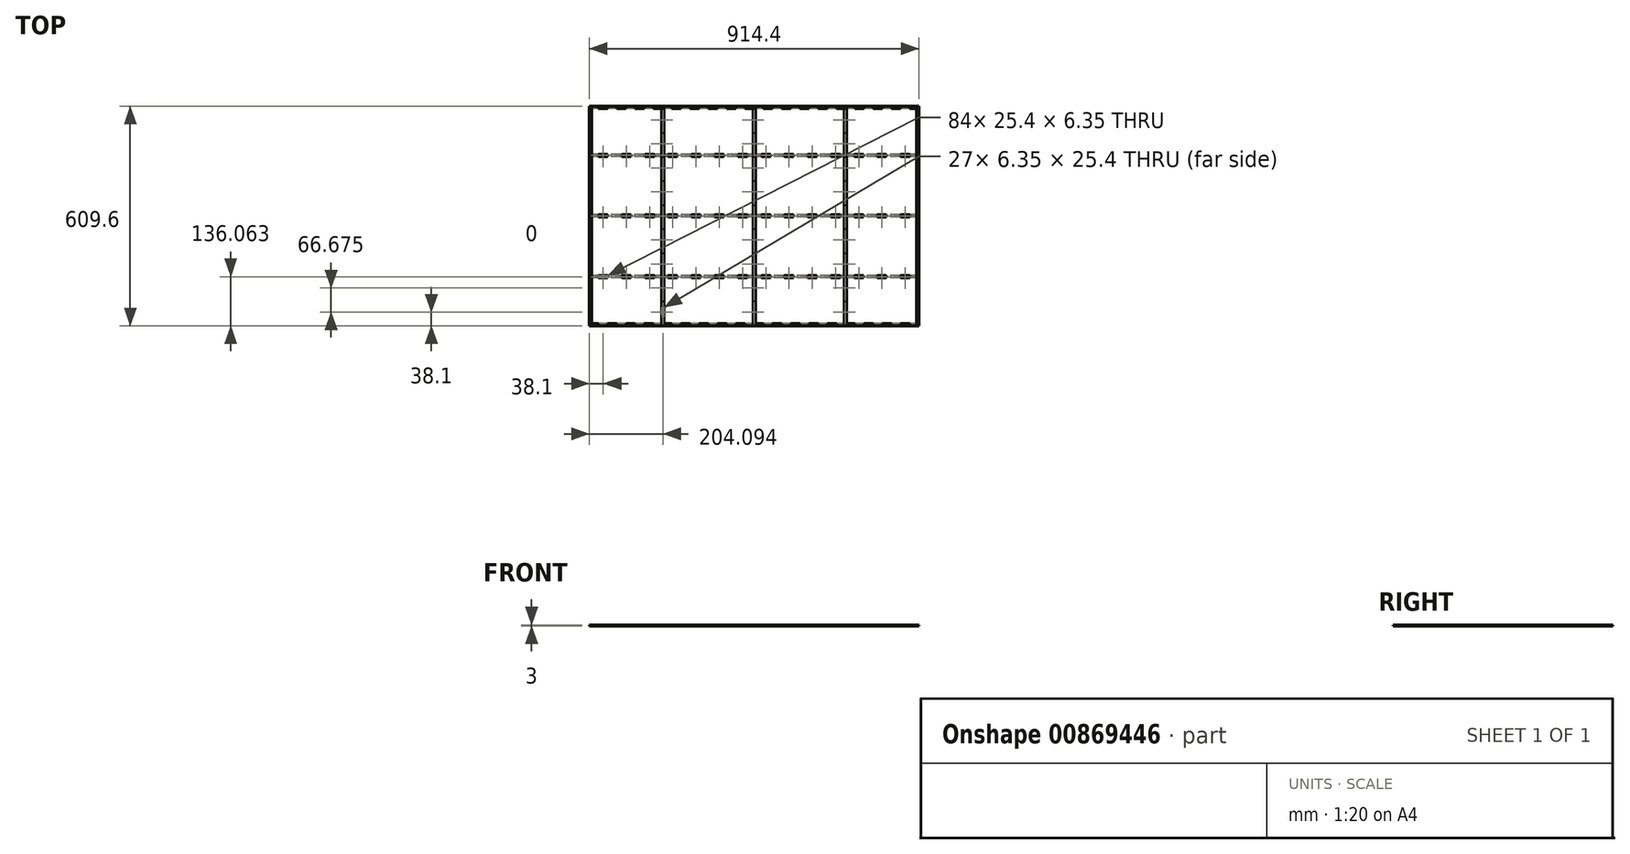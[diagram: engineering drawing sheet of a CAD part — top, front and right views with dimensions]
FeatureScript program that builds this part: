
annotation { "Feature Type Name" : "Feature", "Feature Type Description" : "" }
export const myFeature = defineFeature(function(context is Context, id is Id, definition is map)
    precondition{}
    {
        {
            assignVariable(context, id + "F0", {"name" : "thick", "anyValue" : 0.25});
        }
        {
            assignVariable(context, id + "F1", {"name" : "height", "anyValue" : 3});
        }
        {
            var Q0;
            Q0=qCreatedBy(makeId("Top.planeOp"),FACE);
            var sketch = newSketch(context, id + "F2", { "sketchPlane" : qUnion([Q0])});
            skLineSegment(sketch, "E0.bottom", {"start": v(-457.2, 304.8) * mm, "end": v(457.2, 304.8) * mm, "construction": true});
            skLineSegment(sketch, "E0.top", {"start": v(-457.2, -304.8) * mm, "end": v(457.2, -304.8) * mm, "construction": true});
            skLineSegment(sketch, "E0.left", {"start": v(-457.2, 304.8) * mm, "end": v(-457.2, -304.8) * mm, "construction": true});
            skLineSegment(sketch, "E0.right", {"start": v(457.2, 304.8) * mm, "end": v(457.2, -304.8) * mm, "construction": true});
            skPoint(sketch, "E0.middle", {"position": v(0, 0) * mm});
            skLineSegment(sketch, "E1.bottom", {"start": v(-253.1, 168.74) * mm, "end": v(253.1, 168.74) * mm, "construction": true});
            skLineSegment(sketch, "E1.top", {"start": v(-253.1, -168.74) * mm, "end": v(253.1, -168.74) * mm, "construction": true});
            skLineSegment(sketch, "E1.left", {"start": v(-253.1, 168.74) * mm, "end": v(-253.1, -168.74) * mm, "construction": true});
            skLineSegment(sketch, "E1.right", {"start": v(253.1, 168.74) * mm, "end": v(253.1, -168.74) * mm, "construction": true});
            skLineSegment(sketch, "E2", {"start": v(-457.2, 0) * mm, "end": v(457.2, 0) * mm, "construction": true});
            skLineSegment(sketch, "E3", {"start": v(0, 304.8) * mm, "end": v(0, -304.8) * mm, "construction": true});
            skLineSegment(sketch, "E4", {"start": v(-253.1, 304.8) * mm, "end": v(-253.1, -304.8) * mm, "construction": true});
            skLineSegment(sketch, "E5", {"start": v(253.1, -304.8) * mm, "end": v(253.1, 304.8) * mm, "construction": true});
            skLineSegment(sketch, "E6", {"start": v(457.2, 168.74) * mm, "end": v(-457.2, 168.74) * mm, "construction": true});
            skLineSegment(sketch, "E7", {"start": v(457.2, -168.74) * mm, "end": v(-457.2, -168.74) * mm, "construction": true});
            skSolve(sketch);
        }
        {
            var Q0;
            Q0=qCreatedBy(makeId("Top.planeOp"),FACE);
            var sketch = newSketch(context, id + "F3", { "sketchPlane" : qUnion([Q0])});
            skLineSegment(sketch, "E8.bottom", {"start": v(-256.28, 304.8) * mm, "end": v(-249.93, 304.8) * mm});
            skLineSegment(sketch, "E8.top", {"start": v(-256.28, -304.8) * mm, "end": v(-249.93, -304.8) * mm});
            skLineSegment(sketch, "E8.left", {"start": v(-256.28, 304.8) * mm, "end": v(-256.28, -304.8) * mm});
            skLineSegment(sketch, "E8.right", {"start": v(-249.93, 304.8) * mm, "end": v(-249.93, -304.8) * mm});
            skPoint(sketch, "E8.middle", {"position": v(-253.1, 0) * mm});
            skLineSegment(sketch, "E9.bottom", {"start": v(-3.17, 304.8) * mm, "end": v(3.17, 304.8) * mm});
            skLineSegment(sketch, "E9.top", {"start": v(-3.18, -304.8) * mm, "end": v(3.18, -304.8) * mm});
            skLineSegment(sketch, "E9.left", {"start": v(-3.17, 304.8) * mm, "end": v(-3.18, -304.8) * mm});
            skLineSegment(sketch, "E9.right", {"start": v(3.18, 304.8) * mm, "end": v(3.17, -304.8) * mm});
            skPoint(sketch, "E9.middle", {"position": v(0, 0) * mm});
            skLineSegment(sketch, "E10.bottom", {"start": v(256.28, 304.8) * mm, "end": v(249.93, 304.8) * mm});
            skLineSegment(sketch, "E10.top", {"start": v(256.28, -304.8) * mm, "end": v(249.93, -304.8) * mm});
            skLineSegment(sketch, "E10.left", {"start": v(256.28, 304.8) * mm, "end": v(256.28, -304.8) * mm});
            skLineSegment(sketch, "E10.right", {"start": v(249.93, 304.8) * mm, "end": v(249.93, -304.8) * mm});
            skPoint(sketch, "E10.middle", {"position": v(253.1, 0) * mm});
            skLineSegment(sketch, "E11.bottom", {"start": v(-457.2, 304.8) * mm, "end": v(-450.85, 304.8) * mm});
            skLineSegment(sketch, "E11.top", {"start": v(-457.2, -304.8) * mm, "end": v(-450.85, -304.8) * mm});
            skLineSegment(sketch, "E11.left", {"start": v(-457.2, 304.8) * mm, "end": v(-457.2, -304.8) * mm});
            skLineSegment(sketch, "E11.right", {"start": v(-450.85, 304.8) * mm, "end": v(-450.85, -304.8) * mm});
            skPoint(sketch, "E11.middle", {"position": v(-454.03, 0) * mm});
            skLineSegment(sketch, "E12.bottom", {"start": v(457.2, 304.8) * mm, "end": v(450.85, 304.8) * mm});
            skLineSegment(sketch, "E12.top", {"start": v(457.2, -304.8) * mm, "end": v(450.85, -304.8) * mm});
            skLineSegment(sketch, "E12.left", {"start": v(457.2, 304.8) * mm, "end": v(457.2, -304.8) * mm});
            skLineSegment(sketch, "E12.right", {"start": v(450.85, 304.8) * mm, "end": v(450.85, -304.8) * mm});
            skPoint(sketch, "E12.middle", {"position": v(454.03, 0) * mm});
            skSolve(sketch);
        }
        {
            var Q0;
            Q0=qCreatedBy(makeId("Top.planeOp"),FACE);
            var sketch = newSketch(context, id + "F4", { "sketchPlane" : qUnion([Q0])});
            skLineSegment(sketch, "E13.bottom", {"start": v(-457.2, 298.45) * mm, "end": v(457.2, 298.45) * mm});
            skLineSegment(sketch, "E13.top", {"start": v(-457.2, 304.8) * mm, "end": v(457.2, 304.8) * mm});
            skLineSegment(sketch, "E13.left", {"start": v(-457.2, 298.45) * mm, "end": v(-457.2, 304.8) * mm});
            skLineSegment(sketch, "E13.right", {"start": v(457.2, 298.45) * mm, "end": v(457.2, 304.8) * mm});
            skPoint(sketch, "E13.middle", {"position": v(0, 301.62) * mm});
            skLineSegment(sketch, "E14.bottom", {"start": v(-457.2, 171.91) * mm, "end": v(457.2, 171.91) * mm});
            skLineSegment(sketch, "E14.top", {"start": v(-457.2, 165.56) * mm, "end": v(457.2, 165.56) * mm});
            skLineSegment(sketch, "E14.left", {"start": v(-457.2, 171.91) * mm, "end": v(-457.2, 165.56) * mm});
            skLineSegment(sketch, "E14.right", {"start": v(457.2, 171.91) * mm, "end": v(457.2, 165.56) * mm});
            skPoint(sketch, "E14.middle", {"position": v(0, 168.74) * mm});
            skLineSegment(sketch, "E15.bottom", {"start": v(-457.2, 3.18) * mm, "end": v(457.2, 3.18) * mm});
            skLineSegment(sketch, "E15.top", {"start": v(-457.2, -3.18) * mm, "end": v(457.2, -3.18) * mm});
            skLineSegment(sketch, "E15.left", {"start": v(-457.2, 3.18) * mm, "end": v(-457.2, -3.18) * mm});
            skLineSegment(sketch, "E15.right", {"start": v(457.2, 3.18) * mm, "end": v(457.2, -3.18) * mm});
            skPoint(sketch, "E15.middle", {"position": v(0, 0) * mm});
            skLineSegment(sketch, "E16.bottom", {"start": v(-457.2, -171.91) * mm, "end": v(457.2, -171.91) * mm});
            skLineSegment(sketch, "E16.top", {"start": v(-457.2, -165.56) * mm, "end": v(457.2, -165.56) * mm});
            skLineSegment(sketch, "E16.left", {"start": v(-457.2, -171.91) * mm, "end": v(-457.2, -165.56) * mm});
            skLineSegment(sketch, "E16.right", {"start": v(457.2, -171.91) * mm, "end": v(457.2, -165.56) * mm});
            skPoint(sketch, "E16.middle", {"position": v(0, -168.74) * mm});
            skPoint(sketch, "E16.middle.positionSnap0", {"position": v(0, -3.18) * mm});
            skPoint(sketch, "E16.centerSnap0", {"position": v(0, -3.18) * mm});
            skLineSegment(sketch, "E17.bottom", {"start": v(-457.2, -304.8) * mm, "end": v(457.2, -304.8) * mm});
            skLineSegment(sketch, "E17.top", {"start": v(-457.2, -298.45) * mm, "end": v(457.2, -298.45) * mm});
            skLineSegment(sketch, "E17.left", {"start": v(-457.2, -304.8) * mm, "end": v(-457.2, -298.45) * mm});
            skLineSegment(sketch, "E17.right", {"start": v(457.2, -304.8) * mm, "end": v(457.2, -298.45) * mm});
            skPoint(sketch, "E17.middle", {"position": v(0, -301.62) * mm});
            skSolve(sketch);
        }
        {
            var Q0;
            Q0=qCreatedBy(makeId("Top.planeOp"),FACE);
            var sketch = newSketch(context, id + "F5", { "sketchPlane" : qUnion([Q0])});
            skLineSegment(sketch, "E18.bottom", {"start": v(450.85, 298.45) * mm, "end": v(-450.85, 298.45) * mm});
            skLineSegment(sketch, "E18.top", {"start": v(450.85, -298.45) * mm, "end": v(-450.85, -298.45) * mm});
            skLineSegment(sketch, "E18.left", {"start": v(450.85, 298.45) * mm, "end": v(450.85, -298.45) * mm});
            skLineSegment(sketch, "E18.right", {"start": v(-450.85, 298.45) * mm, "end": v(-450.85, -298.45) * mm});
            skPoint(sketch, "E18.middle", {"position": v(0, 0) * mm});
            skLineSegment(sketch, "E19.bottom", {"start": v(-457.2, 304.8) * mm, "end": v(-431.8, 304.8) * mm});
            skLineSegment(sketch, "E19.top", {"start": v(-457.2, 298.45) * mm, "end": v(-431.8, 298.45) * mm});
            skLineSegment(sketch, "E19.left", {"start": v(-457.2, 304.8) * mm, "end": v(-457.2, 298.45) * mm});
            skLineSegment(sketch, "E19.right", {"start": v(-431.8, 304.8) * mm, "end": v(-431.8, 298.45) * mm});
            skLineSegment(sketch, "E20.1.0.0", {"start": v(-406.4, 304.8) * mm, "end": v(-406.4, 298.45) * mm});
            skLineSegment(sketch, "E20.1.0.1", {"start": v(-406.4, 304.8) * mm, "end": v(-381, 304.8) * mm});
            skLineSegment(sketch, "E20.1.0.2", {"start": v(-381, 304.8) * mm, "end": v(-381, 298.45) * mm});
            skLineSegment(sketch, "E20.1.0.3", {"start": v(-406.4, 298.45) * mm, "end": v(-381, 298.45) * mm});
            skLineSegment(sketch, "E20.2.0.0", {"start": v(-355.6, 304.8) * mm, "end": v(-355.6, 298.45) * mm});
            skLineSegment(sketch, "E20.2.0.1", {"start": v(-355.6, 304.8) * mm, "end": v(-330.2, 304.8) * mm});
            skLineSegment(sketch, "E20.2.0.2", {"start": v(-330.2, 304.8) * mm, "end": v(-330.2, 298.45) * mm});
            skLineSegment(sketch, "E20.2.0.3", {"start": v(-355.6, 298.45) * mm, "end": v(-330.2, 298.45) * mm});
            skLineSegment(sketch, "E20.3.0.0", {"start": v(-304.8, 304.8) * mm, "end": v(-304.8, 298.45) * mm});
            skLineSegment(sketch, "E20.3.0.1", {"start": v(-304.8, 304.8) * mm, "end": v(-279.4, 304.8) * mm});
            skLineSegment(sketch, "E20.3.0.2", {"start": v(-279.4, 304.8) * mm, "end": v(-279.4, 298.45) * mm});
            skLineSegment(sketch, "E20.3.0.3", {"start": v(-304.8, 298.45) * mm, "end": v(-279.4, 298.45) * mm});
            skLineSegment(sketch, "E20.4.0.0", {"start": v(-254, 304.8) * mm, "end": v(-254, 298.45) * mm});
            skLineSegment(sketch, "E20.4.0.1", {"start": v(-254, 304.8) * mm, "end": v(-228.6, 304.8) * mm});
            skLineSegment(sketch, "E20.4.0.2", {"start": v(-228.6, 304.8) * mm, "end": v(-228.6, 298.45) * mm});
            skLineSegment(sketch, "E20.4.0.3", {"start": v(-254, 298.45) * mm, "end": v(-228.6, 298.45) * mm});
            skLineSegment(sketch, "E20.5.0.0", {"start": v(-203.2, 304.8) * mm, "end": v(-203.2, 298.45) * mm});
            skLineSegment(sketch, "E20.5.0.1", {"start": v(-203.2, 304.8) * mm, "end": v(-177.8, 304.8) * mm});
            skLineSegment(sketch, "E20.5.0.2", {"start": v(-177.8, 304.8) * mm, "end": v(-177.8, 298.45) * mm});
            skLineSegment(sketch, "E20.5.0.3", {"start": v(-203.2, 298.45) * mm, "end": v(-177.8, 298.45) * mm});
            skLineSegment(sketch, "E20.6.0.0", {"start": v(-152.4, 304.8) * mm, "end": v(-152.4, 298.45) * mm});
            skLineSegment(sketch, "E20.6.0.1", {"start": v(-152.4, 304.8) * mm, "end": v(-127, 304.8) * mm});
            skLineSegment(sketch, "E20.6.0.2", {"start": v(-127, 304.8) * mm, "end": v(-127, 298.45) * mm});
            skLineSegment(sketch, "E20.6.0.3", {"start": v(-152.4, 298.45) * mm, "end": v(-127, 298.45) * mm});
            skLineSegment(sketch, "E20.7.0.0", {"start": v(-101.6, 304.8) * mm, "end": v(-101.6, 298.45) * mm});
            skLineSegment(sketch, "E20.7.0.1", {"start": v(-101.6, 304.8) * mm, "end": v(-76.2, 304.8) * mm});
            skLineSegment(sketch, "E20.7.0.2", {"start": v(-76.2, 304.8) * mm, "end": v(-76.2, 298.45) * mm});
            skLineSegment(sketch, "E20.7.0.3", {"start": v(-101.6, 298.45) * mm, "end": v(-76.2, 298.45) * mm});
            skLineSegment(sketch, "E20.8.0.0", {"start": v(-50.8, 304.8) * mm, "end": v(-50.8, 298.45) * mm});
            skLineSegment(sketch, "E20.8.0.1", {"start": v(-50.8, 304.8) * mm, "end": v(-25.4, 304.8) * mm});
            skLineSegment(sketch, "E20.8.0.2", {"start": v(-25.4, 304.8) * mm, "end": v(-25.4, 298.45) * mm});
            skLineSegment(sketch, "E20.8.0.3", {"start": v(-50.8, 298.45) * mm, "end": v(-25.4, 298.45) * mm});
            skLineSegment(sketch, "E20.9.0.0", {"start": v(0, 304.8) * mm, "end": v(0, 298.45) * mm});
            skLineSegment(sketch, "E20.9.0.1", {"start": v(0, 304.8) * mm, "end": v(25.4, 304.8) * mm});
            skLineSegment(sketch, "E20.9.0.2", {"start": v(25.4, 304.8) * mm, "end": v(25.4, 298.45) * mm});
            skLineSegment(sketch, "E20.9.0.3", {"start": v(0, 298.45) * mm, "end": v(25.4, 298.45) * mm});
            skLineSegment(sketch, "E20.10.0.0", {"start": v(50.8, 304.8) * mm, "end": v(50.8, 298.45) * mm});
            skLineSegment(sketch, "E20.10.0.1", {"start": v(50.8, 304.8) * mm, "end": v(76.2, 304.8) * mm});
            skLineSegment(sketch, "E20.10.0.2", {"start": v(76.2, 304.8) * mm, "end": v(76.2, 298.45) * mm});
            skLineSegment(sketch, "E20.10.0.3", {"start": v(50.8, 298.45) * mm, "end": v(76.2, 298.45) * mm});
            skLineSegment(sketch, "E20.11.0.0", {"start": v(101.6, 304.8) * mm, "end": v(101.6, 298.45) * mm});
            skLineSegment(sketch, "E20.11.0.1", {"start": v(101.6, 304.8) * mm, "end": v(127, 304.8) * mm});
            skLineSegment(sketch, "E20.11.0.2", {"start": v(127, 304.8) * mm, "end": v(127, 298.45) * mm});
            skLineSegment(sketch, "E20.11.0.3", {"start": v(101.6, 298.45) * mm, "end": v(127, 298.45) * mm});
            skLineSegment(sketch, "E20.12.0.0", {"start": v(152.4, 304.8) * mm, "end": v(152.4, 298.45) * mm});
            skLineSegment(sketch, "E20.12.0.1", {"start": v(152.4, 304.8) * mm, "end": v(177.8, 304.8) * mm});
            skLineSegment(sketch, "E20.12.0.2", {"start": v(177.8, 304.8) * mm, "end": v(177.8, 298.45) * mm});
            skLineSegment(sketch, "E20.12.0.3", {"start": v(152.4, 298.45) * mm, "end": v(177.8, 298.45) * mm});
            skLineSegment(sketch, "E20.13.0.0", {"start": v(203.2, 304.8) * mm, "end": v(203.2, 298.45) * mm});
            skLineSegment(sketch, "E20.13.0.1", {"start": v(203.2, 304.8) * mm, "end": v(228.6, 304.8) * mm});
            skLineSegment(sketch, "E20.13.0.2", {"start": v(228.6, 304.8) * mm, "end": v(228.6, 298.45) * mm});
            skLineSegment(sketch, "E20.13.0.3", {"start": v(203.2, 298.45) * mm, "end": v(228.6, 298.45) * mm});
            skLineSegment(sketch, "E20.14.0.0", {"start": v(254, 304.8) * mm, "end": v(254, 298.45) * mm});
            skLineSegment(sketch, "E20.14.0.1", {"start": v(254, 304.8) * mm, "end": v(279.4, 304.8) * mm});
            skLineSegment(sketch, "E20.14.0.2", {"start": v(279.4, 304.8) * mm, "end": v(279.4, 298.45) * mm});
            skLineSegment(sketch, "E20.14.0.3", {"start": v(254, 298.45) * mm, "end": v(279.4, 298.45) * mm});
            skLineSegment(sketch, "E20.15.0.0", {"start": v(304.8, 304.8) * mm, "end": v(304.8, 298.45) * mm});
            skLineSegment(sketch, "E20.15.0.1", {"start": v(304.8, 304.8) * mm, "end": v(330.2, 304.8) * mm});
            skLineSegment(sketch, "E20.15.0.2", {"start": v(330.2, 304.8) * mm, "end": v(330.2, 298.45) * mm});
            skLineSegment(sketch, "E20.15.0.3", {"start": v(304.8, 298.45) * mm, "end": v(330.2, 298.45) * mm});
            skLineSegment(sketch, "E20.16.0.0", {"start": v(355.6, 304.8) * mm, "end": v(355.6, 298.45) * mm});
            skLineSegment(sketch, "E20.16.0.1", {"start": v(355.6, 304.8) * mm, "end": v(381, 304.8) * mm});
            skLineSegment(sketch, "E20.16.0.2", {"start": v(381, 304.8) * mm, "end": v(381, 298.45) * mm});
            skLineSegment(sketch, "E20.16.0.3", {"start": v(355.6, 298.45) * mm, "end": v(381, 298.45) * mm});
            skLineSegment(sketch, "E20.17.0.0", {"start": v(406.4, 304.8) * mm, "end": v(406.4, 298.45) * mm});
            skLineSegment(sketch, "E20.17.0.1", {"start": v(406.4, 304.8) * mm, "end": v(431.8, 304.8) * mm});
            skLineSegment(sketch, "E20.17.0.2", {"start": v(431.8, 304.8) * mm, "end": v(431.8, 298.45) * mm});
            skLineSegment(sketch, "E20.17.0.3", {"start": v(406.4, 298.45) * mm, "end": v(431.8, 298.45) * mm});
            skLineSegment(sketch, "E20.direction1", {"start": v(-457.2, 298.45) * mm, "end": v(-406.4, 298.45) * mm, "construction": true});
            skLineSegment(sketch, "E21.bottom", {"start": v(450.85, 279.4) * mm, "end": v(457.2, 279.4) * mm});
            skLineSegment(sketch, "E21.top", {"start": v(450.85, 304.8) * mm, "end": v(457.2, 304.8) * mm});
            skLineSegment(sketch, "E21.left", {"start": v(450.85, 279.4) * mm, "end": v(450.85, 304.8) * mm});
            skLineSegment(sketch, "E21.right", {"start": v(457.2, 279.4) * mm, "end": v(457.2, 304.8) * mm});
            skLineSegment(sketch, "E22.0.1.0", {"start": v(450.85, 254) * mm, "end": v(457.2, 254) * mm});
            skLineSegment(sketch, "E22.0.1.1", {"start": v(450.85, 228.6) * mm, "end": v(457.2, 228.6) * mm});
            skLineSegment(sketch, "E22.0.1.2", {"start": v(457.2, 228.6) * mm, "end": v(457.2, 254) * mm});
            skLineSegment(sketch, "E22.0.1.3", {"start": v(450.85, 228.6) * mm, "end": v(450.85, 254) * mm});
            skLineSegment(sketch, "E22.0.2.0", {"start": v(450.85, 203.2) * mm, "end": v(457.2, 203.2) * mm});
            skLineSegment(sketch, "E22.0.2.1", {"start": v(450.85, 177.8) * mm, "end": v(457.2, 177.8) * mm});
            skLineSegment(sketch, "E22.0.2.2", {"start": v(457.2, 177.8) * mm, "end": v(457.2, 203.2) * mm});
            skLineSegment(sketch, "E22.0.2.3", {"start": v(450.85, 177.8) * mm, "end": v(450.85, 203.2) * mm});
            skLineSegment(sketch, "E22.0.3.0", {"start": v(450.85, 152.4) * mm, "end": v(457.2, 152.4) * mm});
            skLineSegment(sketch, "E22.0.3.1", {"start": v(450.85, 127) * mm, "end": v(457.2, 127) * mm});
            skLineSegment(sketch, "E22.0.3.2", {"start": v(457.2, 127) * mm, "end": v(457.2, 152.4) * mm});
            skLineSegment(sketch, "E22.0.3.3", {"start": v(450.85, 127) * mm, "end": v(450.85, 152.4) * mm});
            skLineSegment(sketch, "E22.0.4.0", {"start": v(450.85, 101.6) * mm, "end": v(457.2, 101.6) * mm});
            skLineSegment(sketch, "E22.0.4.1", {"start": v(450.85, 76.2) * mm, "end": v(457.2, 76.2) * mm});
            skLineSegment(sketch, "E22.0.4.2", {"start": v(457.2, 76.2) * mm, "end": v(457.2, 101.6) * mm});
            skLineSegment(sketch, "E22.0.4.3", {"start": v(450.85, 76.2) * mm, "end": v(450.85, 101.6) * mm});
            skLineSegment(sketch, "E22.0.5.0", {"start": v(450.85, 50.8) * mm, "end": v(457.2, 50.8) * mm});
            skLineSegment(sketch, "E22.0.5.1", {"start": v(450.85, 25.4) * mm, "end": v(457.2, 25.4) * mm});
            skLineSegment(sketch, "E22.0.5.2", {"start": v(457.2, 25.4) * mm, "end": v(457.2, 50.8) * mm});
            skLineSegment(sketch, "E22.0.5.3", {"start": v(450.85, 25.4) * mm, "end": v(450.85, 50.8) * mm});
            skLineSegment(sketch, "E22.0.6.0", {"start": v(450.85, 0) * mm, "end": v(457.2, 0) * mm});
            skLineSegment(sketch, "E22.0.6.1", {"start": v(450.85, -25.4) * mm, "end": v(457.2, -25.4) * mm});
            skLineSegment(sketch, "E22.0.6.2", {"start": v(457.2, -25.4) * mm, "end": v(457.2, 0) * mm});
            skLineSegment(sketch, "E22.0.6.3", {"start": v(450.85, -25.4) * mm, "end": v(450.85, 0) * mm});
            skLineSegment(sketch, "E22.0.7.0", {"start": v(450.85, -50.8) * mm, "end": v(457.2, -50.8) * mm});
            skLineSegment(sketch, "E22.0.7.1", {"start": v(450.85, -76.2) * mm, "end": v(457.2, -76.2) * mm});
            skLineSegment(sketch, "E22.0.7.2", {"start": v(457.2, -76.2) * mm, "end": v(457.2, -50.8) * mm});
            skLineSegment(sketch, "E22.0.7.3", {"start": v(450.85, -76.2) * mm, "end": v(450.85, -50.8) * mm});
            skLineSegment(sketch, "E22.0.8.0", {"start": v(450.85, -101.6) * mm, "end": v(457.2, -101.6) * mm});
            skLineSegment(sketch, "E22.0.8.1", {"start": v(450.85, -127) * mm, "end": v(457.2, -127) * mm});
            skLineSegment(sketch, "E22.0.8.2", {"start": v(457.2, -127) * mm, "end": v(457.2, -101.6) * mm});
            skLineSegment(sketch, "E22.0.8.3", {"start": v(450.85, -127) * mm, "end": v(450.85, -101.6) * mm});
            skLineSegment(sketch, "E22.0.9.0", {"start": v(450.85, -152.4) * mm, "end": v(457.2, -152.4) * mm});
            skLineSegment(sketch, "E22.0.9.1", {"start": v(450.85, -177.8) * mm, "end": v(457.2, -177.8) * mm});
            skLineSegment(sketch, "E22.0.9.2", {"start": v(457.2, -177.8) * mm, "end": v(457.2, -152.4) * mm});
            skLineSegment(sketch, "E22.0.9.3", {"start": v(450.85, -177.8) * mm, "end": v(450.85, -152.4) * mm});
            skLineSegment(sketch, "E22.0.10.0", {"start": v(450.85, -203.2) * mm, "end": v(457.2, -203.2) * mm});
            skLineSegment(sketch, "E22.0.10.1", {"start": v(450.85, -228.6) * mm, "end": v(457.2, -228.6) * mm});
            skLineSegment(sketch, "E22.0.10.2", {"start": v(457.2, -228.6) * mm, "end": v(457.2, -203.2) * mm});
            skLineSegment(sketch, "E22.0.10.3", {"start": v(450.85, -228.6) * mm, "end": v(450.85, -203.2) * mm});
            skLineSegment(sketch, "E22.0.11.0", {"start": v(450.85, -254) * mm, "end": v(457.2, -254) * mm});
            skLineSegment(sketch, "E22.0.11.1", {"start": v(450.85, -279.4) * mm, "end": v(457.2, -279.4) * mm});
            skLineSegment(sketch, "E22.0.11.2", {"start": v(457.2, -279.4) * mm, "end": v(457.2, -254) * mm});
            skLineSegment(sketch, "E22.0.11.3", {"start": v(450.85, -279.4) * mm, "end": v(450.85, -254) * mm});
            skLineSegment(sketch, "E22.direction1", {"start": v(450.85, 279.4) * mm, "end": v(476.25, 279.4) * mm, "construction": true});
            skLineSegment(sketch, "E22.direction2", {"start": v(450.85, 279.4) * mm, "end": v(450.85, 228.6) * mm, "construction": true});
            skLineSegment(sketch, "E23.bottom", {"start": v(431.8, -304.8) * mm, "end": v(457.2, -304.8) * mm});
            skLineSegment(sketch, "E23.top", {"start": v(431.8, -298.45) * mm, "end": v(457.2, -298.45) * mm});
            skLineSegment(sketch, "E23.left", {"start": v(431.8, -304.8) * mm, "end": v(431.8, -298.45) * mm});
            skLineSegment(sketch, "E23.right", {"start": v(457.2, -304.8) * mm, "end": v(457.2, -298.45) * mm});
            skLineSegment(sketch, "E24.1.0.0", {"start": v(406.4, -304.8) * mm, "end": v(406.4, -298.45) * mm});
            skLineSegment(sketch, "E24.1.0.1", {"start": v(381, -304.8) * mm, "end": v(381, -298.45) * mm});
            skLineSegment(sketch, "E24.1.0.2", {"start": v(381, -298.45) * mm, "end": v(406.4, -298.45) * mm});
            skLineSegment(sketch, "E24.1.0.3", {"start": v(381, -304.8) * mm, "end": v(406.4, -304.8) * mm});
            skLineSegment(sketch, "E24.2.0.0", {"start": v(355.6, -304.8) * mm, "end": v(355.6, -298.45) * mm});
            skLineSegment(sketch, "E24.2.0.1", {"start": v(330.2, -304.8) * mm, "end": v(330.2, -298.45) * mm});
            skLineSegment(sketch, "E24.2.0.2", {"start": v(330.2, -298.45) * mm, "end": v(355.6, -298.45) * mm});
            skLineSegment(sketch, "E24.2.0.3", {"start": v(330.2, -304.8) * mm, "end": v(355.6, -304.8) * mm});
            skLineSegment(sketch, "E24.3.0.0", {"start": v(304.8, -304.8) * mm, "end": v(304.8, -298.45) * mm});
            skLineSegment(sketch, "E24.3.0.1", {"start": v(279.4, -304.8) * mm, "end": v(279.4, -298.45) * mm});
            skLineSegment(sketch, "E24.3.0.2", {"start": v(279.4, -298.45) * mm, "end": v(304.8, -298.45) * mm});
            skLineSegment(sketch, "E24.3.0.3", {"start": v(279.4, -304.8) * mm, "end": v(304.8, -304.8) * mm});
            skLineSegment(sketch, "E24.4.0.0", {"start": v(254, -304.8) * mm, "end": v(254, -298.45) * mm});
            skLineSegment(sketch, "E24.4.0.1", {"start": v(228.6, -304.8) * mm, "end": v(228.6, -298.45) * mm});
            skLineSegment(sketch, "E24.4.0.2", {"start": v(228.6, -298.45) * mm, "end": v(254, -298.45) * mm});
            skLineSegment(sketch, "E24.4.0.3", {"start": v(228.6, -304.8) * mm, "end": v(254, -304.8) * mm});
            skLineSegment(sketch, "E24.5.0.0", {"start": v(203.2, -304.8) * mm, "end": v(203.2, -298.45) * mm});
            skLineSegment(sketch, "E24.5.0.1", {"start": v(177.8, -304.8) * mm, "end": v(177.8, -298.45) * mm});
            skLineSegment(sketch, "E24.5.0.2", {"start": v(177.8, -298.45) * mm, "end": v(203.2, -298.45) * mm});
            skLineSegment(sketch, "E24.5.0.3", {"start": v(177.8, -304.8) * mm, "end": v(203.2, -304.8) * mm});
            skLineSegment(sketch, "E24.6.0.0", {"start": v(152.4, -304.8) * mm, "end": v(152.4, -298.45) * mm});
            skLineSegment(sketch, "E24.6.0.1", {"start": v(127, -304.8) * mm, "end": v(127, -298.45) * mm});
            skLineSegment(sketch, "E24.6.0.2", {"start": v(127, -298.45) * mm, "end": v(152.4, -298.45) * mm});
            skLineSegment(sketch, "E24.6.0.3", {"start": v(127, -304.8) * mm, "end": v(152.4, -304.8) * mm});
            skLineSegment(sketch, "E24.7.0.0", {"start": v(101.6, -304.8) * mm, "end": v(101.6, -298.45) * mm});
            skLineSegment(sketch, "E24.7.0.1", {"start": v(76.2, -304.8) * mm, "end": v(76.2, -298.45) * mm});
            skLineSegment(sketch, "E24.7.0.2", {"start": v(76.2, -298.45) * mm, "end": v(101.6, -298.45) * mm});
            skLineSegment(sketch, "E24.7.0.3", {"start": v(76.2, -304.8) * mm, "end": v(101.6, -304.8) * mm});
            skLineSegment(sketch, "E24.8.0.0", {"start": v(50.8, -304.8) * mm, "end": v(50.8, -298.45) * mm});
            skLineSegment(sketch, "E24.8.0.1", {"start": v(25.4, -304.8) * mm, "end": v(25.4, -298.45) * mm});
            skLineSegment(sketch, "E24.8.0.2", {"start": v(25.4, -298.45) * mm, "end": v(50.8, -298.45) * mm});
            skLineSegment(sketch, "E24.8.0.3", {"start": v(25.4, -304.8) * mm, "end": v(50.8, -304.8) * mm});
            skLineSegment(sketch, "E24.9.0.0", {"start": v(0, -304.8) * mm, "end": v(0, -298.45) * mm});
            skLineSegment(sketch, "E24.9.0.1", {"start": v(-25.4, -304.8) * mm, "end": v(-25.4, -298.45) * mm});
            skLineSegment(sketch, "E24.9.0.2", {"start": v(-25.4, -298.45) * mm, "end": v(0, -298.45) * mm});
            skLineSegment(sketch, "E24.9.0.3", {"start": v(-25.4, -304.8) * mm, "end": v(0, -304.8) * mm});
            skLineSegment(sketch, "E24.10.0.0", {"start": v(-50.8, -304.8) * mm, "end": v(-50.8, -298.45) * mm});
            skLineSegment(sketch, "E24.10.0.1", {"start": v(-76.2, -304.8) * mm, "end": v(-76.2, -298.45) * mm});
            skLineSegment(sketch, "E24.10.0.2", {"start": v(-76.2, -298.45) * mm, "end": v(-50.8, -298.45) * mm});
            skLineSegment(sketch, "E24.10.0.3", {"start": v(-76.2, -304.8) * mm, "end": v(-50.8, -304.8) * mm});
            skLineSegment(sketch, "E24.11.0.0", {"start": v(-101.6, -304.8) * mm, "end": v(-101.6, -298.45) * mm});
            skLineSegment(sketch, "E24.11.0.1", {"start": v(-127, -304.8) * mm, "end": v(-127, -298.45) * mm});
            skLineSegment(sketch, "E24.11.0.2", {"start": v(-127, -298.45) * mm, "end": v(-101.6, -298.45) * mm});
            skLineSegment(sketch, "E24.11.0.3", {"start": v(-127, -304.8) * mm, "end": v(-101.6, -304.8) * mm});
            skLineSegment(sketch, "E24.12.0.0", {"start": v(-152.4, -304.8) * mm, "end": v(-152.4, -298.45) * mm});
            skLineSegment(sketch, "E24.12.0.1", {"start": v(-177.8, -304.8) * mm, "end": v(-177.8, -298.45) * mm});
            skLineSegment(sketch, "E24.12.0.2", {"start": v(-177.8, -298.45) * mm, "end": v(-152.4, -298.45) * mm});
            skLineSegment(sketch, "E24.12.0.3", {"start": v(-177.8, -304.8) * mm, "end": v(-152.4, -304.8) * mm});
            skLineSegment(sketch, "E24.13.0.0", {"start": v(-203.2, -304.8) * mm, "end": v(-203.2, -298.45) * mm});
            skLineSegment(sketch, "E24.13.0.1", {"start": v(-228.6, -304.8) * mm, "end": v(-228.6, -298.45) * mm});
            skLineSegment(sketch, "E24.13.0.2", {"start": v(-228.6, -298.45) * mm, "end": v(-203.2, -298.45) * mm});
            skLineSegment(sketch, "E24.13.0.3", {"start": v(-228.6, -304.8) * mm, "end": v(-203.2, -304.8) * mm});
            skLineSegment(sketch, "E24.14.0.0", {"start": v(-254, -304.8) * mm, "end": v(-254, -298.45) * mm});
            skLineSegment(sketch, "E24.14.0.1", {"start": v(-279.4, -304.8) * mm, "end": v(-279.4, -298.45) * mm});
            skLineSegment(sketch, "E24.14.0.2", {"start": v(-279.4, -298.45) * mm, "end": v(-254, -298.45) * mm});
            skLineSegment(sketch, "E24.14.0.3", {"start": v(-279.4, -304.8) * mm, "end": v(-254, -304.8) * mm});
            skLineSegment(sketch, "E24.15.0.0", {"start": v(-304.8, -304.8) * mm, "end": v(-304.8, -298.45) * mm});
            skLineSegment(sketch, "E24.15.0.1", {"start": v(-330.2, -304.8) * mm, "end": v(-330.2, -298.45) * mm});
            skLineSegment(sketch, "E24.15.0.2", {"start": v(-330.2, -298.45) * mm, "end": v(-304.8, -298.45) * mm});
            skLineSegment(sketch, "E24.15.0.3", {"start": v(-330.2, -304.8) * mm, "end": v(-304.8, -304.8) * mm});
            skLineSegment(sketch, "E24.16.0.0", {"start": v(-355.6, -304.8) * mm, "end": v(-355.6, -298.45) * mm});
            skLineSegment(sketch, "E24.16.0.1", {"start": v(-381, -304.8) * mm, "end": v(-381, -298.45) * mm});
            skLineSegment(sketch, "E24.16.0.2", {"start": v(-381, -298.45) * mm, "end": v(-355.6, -298.45) * mm});
            skLineSegment(sketch, "E24.16.0.3", {"start": v(-381, -304.8) * mm, "end": v(-355.6, -304.8) * mm});
            skLineSegment(sketch, "E24.17.0.0", {"start": v(-406.4, -304.8) * mm, "end": v(-406.4, -298.45) * mm});
            skLineSegment(sketch, "E24.17.0.1", {"start": v(-431.8, -304.8) * mm, "end": v(-431.8, -298.45) * mm});
            skLineSegment(sketch, "E24.17.0.2", {"start": v(-431.8, -298.45) * mm, "end": v(-406.4, -298.45) * mm});
            skLineSegment(sketch, "E24.17.0.3", {"start": v(-431.8, -304.8) * mm, "end": v(-406.4, -304.8) * mm});
            skLineSegment(sketch, "E24.direction1", {"start": v(431.8, -304.8) * mm, "end": v(381, -304.8) * mm, "construction": true});
            skLineSegment(sketch, "E25.bottom", {"start": v(-457.2, -304.8) * mm, "end": v(-450.85, -304.8) * mm});
            skLineSegment(sketch, "E25.top", {"start": v(-457.2, -279.4) * mm, "end": v(-450.85, -279.4) * mm});
            skLineSegment(sketch, "E25.left", {"start": v(-457.2, -304.8) * mm, "end": v(-457.2, -279.4) * mm});
            skLineSegment(sketch, "E25.right", {"start": v(-450.85, -304.8) * mm, "end": v(-450.85, -279.4) * mm});
            skLineSegment(sketch, "E26.0.1.0", {"start": v(-450.85, -254) * mm, "end": v(-450.85, -228.6) * mm});
            skLineSegment(sketch, "E26.0.1.1", {"start": v(-457.2, -254) * mm, "end": v(-457.2, -228.6) * mm});
            skLineSegment(sketch, "E26.0.1.2", {"start": v(-457.2, -254) * mm, "end": v(-450.85, -254) * mm});
            skLineSegment(sketch, "E26.0.1.3", {"start": v(-457.2, -228.6) * mm, "end": v(-450.85, -228.6) * mm});
            skLineSegment(sketch, "E26.0.2.0", {"start": v(-450.85, -203.2) * mm, "end": v(-450.85, -177.8) * mm});
            skLineSegment(sketch, "E26.0.2.1", {"start": v(-457.2, -203.2) * mm, "end": v(-457.2, -177.8) * mm});
            skLineSegment(sketch, "E26.0.2.2", {"start": v(-457.2, -203.2) * mm, "end": v(-450.85, -203.2) * mm});
            skLineSegment(sketch, "E26.0.2.3", {"start": v(-457.2, -177.8) * mm, "end": v(-450.85, -177.8) * mm});
            skLineSegment(sketch, "E26.0.3.0", {"start": v(-450.85, -152.4) * mm, "end": v(-450.85, -127) * mm});
            skLineSegment(sketch, "E26.0.3.1", {"start": v(-457.2, -152.4) * mm, "end": v(-457.2, -127) * mm});
            skLineSegment(sketch, "E26.0.3.2", {"start": v(-457.2, -152.4) * mm, "end": v(-450.85, -152.4) * mm});
            skLineSegment(sketch, "E26.0.3.3", {"start": v(-457.2, -127) * mm, "end": v(-450.85, -127) * mm});
            skLineSegment(sketch, "E26.0.4.0", {"start": v(-450.85, -101.6) * mm, "end": v(-450.85, -76.2) * mm});
            skLineSegment(sketch, "E26.0.4.1", {"start": v(-457.2, -101.6) * mm, "end": v(-457.2, -76.2) * mm});
            skLineSegment(sketch, "E26.0.4.2", {"start": v(-457.2, -101.6) * mm, "end": v(-450.85, -101.6) * mm});
            skLineSegment(sketch, "E26.0.4.3", {"start": v(-457.2, -76.2) * mm, "end": v(-450.85, -76.2) * mm});
            skLineSegment(sketch, "E26.0.5.0", {"start": v(-450.85, -50.8) * mm, "end": v(-450.85, -25.4) * mm});
            skLineSegment(sketch, "E26.0.5.1", {"start": v(-457.2, -50.8) * mm, "end": v(-457.2, -25.4) * mm});
            skLineSegment(sketch, "E26.0.5.2", {"start": v(-457.2, -50.8) * mm, "end": v(-450.85, -50.8) * mm});
            skLineSegment(sketch, "E26.0.5.3", {"start": v(-457.2, -25.4) * mm, "end": v(-450.85, -25.4) * mm});
            skLineSegment(sketch, "E26.0.6.0", {"start": v(-450.85, 0) * mm, "end": v(-450.85, 25.4) * mm});
            skLineSegment(sketch, "E26.0.6.1", {"start": v(-457.2, 0) * mm, "end": v(-457.2, 25.4) * mm});
            skLineSegment(sketch, "E26.0.6.2", {"start": v(-457.2, 0) * mm, "end": v(-450.85, 0) * mm});
            skLineSegment(sketch, "E26.0.6.3", {"start": v(-457.2, 25.4) * mm, "end": v(-450.85, 25.4) * mm});
            skLineSegment(sketch, "E26.0.7.0", {"start": v(-450.85, 50.8) * mm, "end": v(-450.85, 76.2) * mm});
            skLineSegment(sketch, "E26.0.7.1", {"start": v(-457.2, 50.8) * mm, "end": v(-457.2, 76.2) * mm});
            skLineSegment(sketch, "E26.0.7.2", {"start": v(-457.2, 50.8) * mm, "end": v(-450.85, 50.8) * mm});
            skLineSegment(sketch, "E26.0.7.3", {"start": v(-457.2, 76.2) * mm, "end": v(-450.85, 76.2) * mm});
            skLineSegment(sketch, "E26.0.8.0", {"start": v(-450.85, 101.6) * mm, "end": v(-450.85, 127) * mm});
            skLineSegment(sketch, "E26.0.8.1", {"start": v(-457.2, 101.6) * mm, "end": v(-457.2, 127) * mm});
            skLineSegment(sketch, "E26.0.8.2", {"start": v(-457.2, 101.6) * mm, "end": v(-450.85, 101.6) * mm});
            skLineSegment(sketch, "E26.0.8.3", {"start": v(-457.2, 127) * mm, "end": v(-450.85, 127) * mm});
            skLineSegment(sketch, "E26.0.9.0", {"start": v(-450.85, 152.4) * mm, "end": v(-450.85, 177.8) * mm});
            skLineSegment(sketch, "E26.0.9.1", {"start": v(-457.2, 152.4) * mm, "end": v(-457.2, 177.8) * mm});
            skLineSegment(sketch, "E26.0.9.2", {"start": v(-457.2, 152.4) * mm, "end": v(-450.85, 152.4) * mm});
            skLineSegment(sketch, "E26.0.9.3", {"start": v(-457.2, 177.8) * mm, "end": v(-450.85, 177.8) * mm});
            skLineSegment(sketch, "E26.0.10.0", {"start": v(-450.85, 203.2) * mm, "end": v(-450.85, 228.6) * mm});
            skLineSegment(sketch, "E26.0.10.1", {"start": v(-457.2, 203.2) * mm, "end": v(-457.2, 228.6) * mm});
            skLineSegment(sketch, "E26.0.10.2", {"start": v(-457.2, 203.2) * mm, "end": v(-450.85, 203.2) * mm});
            skLineSegment(sketch, "E26.0.10.3", {"start": v(-457.2, 228.6) * mm, "end": v(-450.85, 228.6) * mm});
            skLineSegment(sketch, "E26.0.11.0", {"start": v(-450.85, 254) * mm, "end": v(-450.85, 279.4) * mm});
            skLineSegment(sketch, "E26.0.11.1", {"start": v(-457.2, 254) * mm, "end": v(-457.2, 279.4) * mm});
            skLineSegment(sketch, "E26.0.11.2", {"start": v(-457.2, 254) * mm, "end": v(-450.85, 254) * mm});
            skLineSegment(sketch, "E26.0.11.3", {"start": v(-457.2, 279.4) * mm, "end": v(-450.85, 279.4) * mm});
            skLineSegment(sketch, "E26.direction1", {"start": v(-457.2, -304.8) * mm, "end": v(-431.8, -304.8) * mm, "construction": true});
            skLineSegment(sketch, "E26.direction2", {"start": v(-457.2, -304.8) * mm, "end": v(-457.2, -254) * mm, "construction": true});
            skSolve(sketch);
        }
        {
            var Q0;
            Q0=qCreatedBy(makeId("Top.planeOp"),FACE);
            var sketch = newSketch(context, id + "F6", { "sketchPlane" : qUnion([Q0])});
            skLineSegment(sketch, "E27.bottom", {"start": v(-256.28, 279.4) * mm, "end": v(-249.93, 279.4) * mm});
            skLineSegment(sketch, "E27.top", {"start": v(-256.28, 254) * mm, "end": v(-249.93, 254) * mm});
            skLineSegment(sketch, "E27.left", {"start": v(-256.28, 279.4) * mm, "end": v(-256.28, 254) * mm});
            skLineSegment(sketch, "E27.right", {"start": v(-249.93, 279.4) * mm, "end": v(-249.93, 254) * mm});
            skLineSegment(sketch, "E28.0.1.0", {"start": v(-256.28, 212.73) * mm, "end": v(-256.28, 187.32) * mm});
            skLineSegment(sketch, "E28.0.1.1", {"start": v(-256.28, 187.33) * mm, "end": v(-249.93, 187.33) * mm});
            skLineSegment(sketch, "E28.0.1.2", {"start": v(-249.93, 212.73) * mm, "end": v(-249.93, 187.33) * mm});
            skLineSegment(sketch, "E28.0.1.3", {"start": v(-256.28, 212.73) * mm, "end": v(-249.93, 212.73) * mm});
            skLineSegment(sketch, "E28.0.2.0", {"start": v(-256.28, 146.05) * mm, "end": v(-256.28, 120.65) * mm});
            skLineSegment(sketch, "E28.0.2.1", {"start": v(-256.28, 120.65) * mm, "end": v(-249.93, 120.65) * mm});
            skLineSegment(sketch, "E28.0.2.2", {"start": v(-249.93, 146.05) * mm, "end": v(-249.93, 120.65) * mm});
            skLineSegment(sketch, "E28.0.2.3", {"start": v(-256.28, 146.05) * mm, "end": v(-249.93, 146.05) * mm});
            skLineSegment(sketch, "E28.0.3.0", {"start": v(-256.28, 79.38) * mm, "end": v(-256.28, 53.97) * mm});
            skLineSegment(sketch, "E28.0.3.1", {"start": v(-256.28, 53.98) * mm, "end": v(-249.93, 53.98) * mm});
            skLineSegment(sketch, "E28.0.3.2", {"start": v(-249.93, 79.38) * mm, "end": v(-249.93, 53.98) * mm});
            skLineSegment(sketch, "E28.0.3.3", {"start": v(-256.28, 79.38) * mm, "end": v(-249.93, 79.38) * mm});
            skLineSegment(sketch, "E28.0.4.0", {"start": v(-256.28, 12.7) * mm, "end": v(-256.28, -12.7) * mm});
            skLineSegment(sketch, "E28.0.4.1", {"start": v(-256.28, -12.7) * mm, "end": v(-249.93, -12.7) * mm});
            skLineSegment(sketch, "E28.0.4.2", {"start": v(-249.93, 12.7) * mm, "end": v(-249.93, -12.7) * mm});
            skLineSegment(sketch, "E28.0.4.3", {"start": v(-256.28, 12.7) * mm, "end": v(-249.93, 12.7) * mm});
            skLineSegment(sketch, "E28.0.5.0", {"start": v(-256.28, -53.98) * mm, "end": v(-256.28, -79.38) * mm});
            skLineSegment(sketch, "E28.0.5.1", {"start": v(-256.28, -79.38) * mm, "end": v(-249.93, -79.38) * mm});
            skLineSegment(sketch, "E28.0.5.2", {"start": v(-249.93, -53.98) * mm, "end": v(-249.93, -79.38) * mm});
            skLineSegment(sketch, "E28.0.5.3", {"start": v(-256.28, -53.98) * mm, "end": v(-249.93, -53.98) * mm});
            skLineSegment(sketch, "E28.0.6.0", {"start": v(-256.28, -120.65) * mm, "end": v(-256.28, -146.05) * mm});
            skLineSegment(sketch, "E28.0.6.1", {"start": v(-256.28, -146.05) * mm, "end": v(-249.93, -146.05) * mm});
            skLineSegment(sketch, "E28.0.6.2", {"start": v(-249.93, -120.65) * mm, "end": v(-249.93, -146.05) * mm});
            skLineSegment(sketch, "E28.0.6.3", {"start": v(-256.28, -120.65) * mm, "end": v(-249.93, -120.65) * mm});
            skLineSegment(sketch, "E28.1.0.0", {"start": v(-3.17, 279.4) * mm, "end": v(-3.17, 254) * mm});
            skLineSegment(sketch, "E28.1.0.1", {"start": v(-3.18, 254) * mm, "end": v(3.17, 254) * mm});
            skLineSegment(sketch, "E28.1.0.2", {"start": v(3.17, 279.4) * mm, "end": v(3.17, 254) * mm});
            skLineSegment(sketch, "E28.1.0.3", {"start": v(-3.18, 279.4) * mm, "end": v(3.17, 279.4) * mm});
            skLineSegment(sketch, "E28.1.1.0", {"start": v(-3.17, 212.73) * mm, "end": v(-3.17, 187.32) * mm});
            skLineSegment(sketch, "E28.1.1.1", {"start": v(-3.18, 187.33) * mm, "end": v(3.17, 187.33) * mm});
            skLineSegment(sketch, "E28.1.1.2", {"start": v(3.17, 212.73) * mm, "end": v(3.17, 187.33) * mm});
            skLineSegment(sketch, "E28.1.1.3", {"start": v(-3.18, 212.73) * mm, "end": v(3.17, 212.73) * mm});
            skLineSegment(sketch, "E28.1.2.0", {"start": v(-3.17, 146.05) * mm, "end": v(-3.17, 120.65) * mm});
            skLineSegment(sketch, "E28.1.2.1", {"start": v(-3.18, 120.65) * mm, "end": v(3.17, 120.65) * mm});
            skLineSegment(sketch, "E28.1.2.2", {"start": v(3.17, 146.05) * mm, "end": v(3.17, 120.65) * mm});
            skLineSegment(sketch, "E28.1.2.3", {"start": v(-3.18, 146.05) * mm, "end": v(3.17, 146.05) * mm});
            skLineSegment(sketch, "E28.1.3.0", {"start": v(-3.17, 79.38) * mm, "end": v(-3.17, 53.97) * mm});
            skLineSegment(sketch, "E28.1.3.1", {"start": v(-3.18, 53.98) * mm, "end": v(3.17, 53.98) * mm});
            skLineSegment(sketch, "E28.1.3.2", {"start": v(3.17, 79.38) * mm, "end": v(3.17, 53.98) * mm});
            skLineSegment(sketch, "E28.1.3.3", {"start": v(-3.18, 79.38) * mm, "end": v(3.17, 79.38) * mm});
            skLineSegment(sketch, "E28.1.4.0", {"start": v(-3.17, 12.7) * mm, "end": v(-3.17, -12.7) * mm});
            skLineSegment(sketch, "E28.1.4.1", {"start": v(-3.18, -12.7) * mm, "end": v(3.17, -12.7) * mm});
            skLineSegment(sketch, "E28.1.4.2", {"start": v(3.17, 12.7) * mm, "end": v(3.17, -12.7) * mm});
            skLineSegment(sketch, "E28.1.4.3", {"start": v(-3.18, 12.7) * mm, "end": v(3.17, 12.7) * mm});
            skLineSegment(sketch, "E28.1.5.0", {"start": v(-3.17, -53.98) * mm, "end": v(-3.17, -79.38) * mm});
            skLineSegment(sketch, "E28.1.5.1", {"start": v(-3.18, -79.38) * mm, "end": v(3.17, -79.38) * mm});
            skLineSegment(sketch, "E28.1.5.2", {"start": v(3.17, -53.98) * mm, "end": v(3.17, -79.38) * mm});
            skLineSegment(sketch, "E28.1.5.3", {"start": v(-3.18, -53.98) * mm, "end": v(3.17, -53.98) * mm});
            skLineSegment(sketch, "E28.1.6.0", {"start": v(-3.17, -120.65) * mm, "end": v(-3.17, -146.05) * mm});
            skLineSegment(sketch, "E28.1.6.1", {"start": v(-3.18, -146.05) * mm, "end": v(3.17, -146.05) * mm});
            skLineSegment(sketch, "E28.1.6.2", {"start": v(3.17, -120.65) * mm, "end": v(3.17, -146.05) * mm});
            skLineSegment(sketch, "E28.1.6.3", {"start": v(-3.18, -120.65) * mm, "end": v(3.17, -120.65) * mm});
            skLineSegment(sketch, "E28.2.0.0", {"start": v(249.93, 279.4) * mm, "end": v(249.93, 254) * mm});
            skLineSegment(sketch, "E28.2.0.1", {"start": v(249.93, 254) * mm, "end": v(256.28, 254) * mm});
            skLineSegment(sketch, "E28.2.0.2", {"start": v(256.28, 279.4) * mm, "end": v(256.28, 254) * mm});
            skLineSegment(sketch, "E28.2.0.3", {"start": v(249.93, 279.4) * mm, "end": v(256.28, 279.4) * mm});
            skLineSegment(sketch, "E28.2.1.0", {"start": v(249.93, 212.73) * mm, "end": v(249.93, 187.32) * mm});
            skLineSegment(sketch, "E28.2.1.1", {"start": v(249.93, 187.33) * mm, "end": v(256.28, 187.33) * mm});
            skLineSegment(sketch, "E28.2.1.2", {"start": v(256.28, 212.73) * mm, "end": v(256.28, 187.33) * mm});
            skLineSegment(sketch, "E28.2.1.3", {"start": v(249.93, 212.73) * mm, "end": v(256.28, 212.73) * mm});
            skLineSegment(sketch, "E28.2.2.0", {"start": v(249.93, 146.05) * mm, "end": v(249.93, 120.65) * mm});
            skLineSegment(sketch, "E28.2.2.1", {"start": v(249.93, 120.65) * mm, "end": v(256.28, 120.65) * mm});
            skLineSegment(sketch, "E28.2.2.2", {"start": v(256.28, 146.05) * mm, "end": v(256.28, 120.65) * mm});
            skLineSegment(sketch, "E28.2.2.3", {"start": v(249.93, 146.05) * mm, "end": v(256.28, 146.05) * mm});
            skLineSegment(sketch, "E28.2.3.0", {"start": v(249.93, 79.38) * mm, "end": v(249.93, 53.97) * mm});
            skLineSegment(sketch, "E28.2.3.1", {"start": v(249.93, 53.98) * mm, "end": v(256.28, 53.98) * mm});
            skLineSegment(sketch, "E28.2.3.2", {"start": v(256.28, 79.38) * mm, "end": v(256.28, 53.98) * mm});
            skLineSegment(sketch, "E28.2.3.3", {"start": v(249.93, 79.38) * mm, "end": v(256.28, 79.38) * mm});
            skLineSegment(sketch, "E28.2.4.0", {"start": v(249.93, 12.7) * mm, "end": v(249.93, -12.7) * mm});
            skLineSegment(sketch, "E28.2.4.1", {"start": v(249.93, -12.7) * mm, "end": v(256.28, -12.7) * mm});
            skLineSegment(sketch, "E28.2.4.2", {"start": v(256.28, 12.7) * mm, "end": v(256.28, -12.7) * mm});
            skLineSegment(sketch, "E28.2.4.3", {"start": v(249.93, 12.7) * mm, "end": v(256.28, 12.7) * mm});
            skLineSegment(sketch, "E28.2.5.0", {"start": v(249.93, -53.98) * mm, "end": v(249.93, -79.38) * mm});
            skLineSegment(sketch, "E28.2.5.1", {"start": v(249.93, -79.38) * mm, "end": v(256.28, -79.38) * mm});
            skLineSegment(sketch, "E28.2.5.2", {"start": v(256.28, -53.98) * mm, "end": v(256.28, -79.38) * mm});
            skLineSegment(sketch, "E28.2.5.3", {"start": v(249.93, -53.98) * mm, "end": v(256.28, -53.98) * mm});
            skLineSegment(sketch, "E28.2.6.0", {"start": v(249.93, -120.65) * mm, "end": v(249.93, -146.05) * mm});
            skLineSegment(sketch, "E28.2.6.1", {"start": v(249.93, -146.05) * mm, "end": v(256.28, -146.05) * mm});
            skLineSegment(sketch, "E28.2.6.2", {"start": v(256.28, -120.65) * mm, "end": v(256.28, -146.05) * mm});
            skLineSegment(sketch, "E28.2.6.3", {"start": v(249.93, -120.65) * mm, "end": v(256.28, -120.65) * mm});
            skLineSegment(sketch, "E28.direction1", {"start": v(-256.28, 254) * mm, "end": v(-3.18, 254) * mm, "construction": true});
            skLineSegment(sketch, "E28.direction2", {"start": v(-256.28, 254) * mm, "end": v(-256.28, 187.32) * mm, "construction": true});
            skLineSegment(sketch, "E29.0.0.7", {"start": v(-256.28, -187.33) * mm, "end": v(-256.28, -212.73) * mm});
            skLineSegment(sketch, "E29.3.0.7", {"start": v(-256.28, -212.72) * mm, "end": v(-249.93, -212.72) * mm});
            skLineSegment(sketch, "E29.6.0.7", {"start": v(-249.93, -187.33) * mm, "end": v(-249.93, -212.72) * mm});
            skLineSegment(sketch, "E29.9.0.7", {"start": v(-256.28, -187.33) * mm, "end": v(-249.93, -187.33) * mm});
            skLineSegment(sketch, "E29.0.0.8", {"start": v(-256.28, -254) * mm, "end": v(-256.28, -279.4) * mm});
            skLineSegment(sketch, "E29.3.0.8", {"start": v(-256.28, -279.4) * mm, "end": v(-249.93, -279.4) * mm});
            skLineSegment(sketch, "E29.6.0.8", {"start": v(-249.93, -254) * mm, "end": v(-249.93, -279.4) * mm});
            skLineSegment(sketch, "E29.9.0.8", {"start": v(-256.28, -254) * mm, "end": v(-249.93, -254) * mm});
            skLineSegment(sketch, "E29.0.1.7", {"start": v(-3.17, -187.33) * mm, "end": v(-3.17, -212.73) * mm});
            skLineSegment(sketch, "E29.3.1.7", {"start": v(-3.18, -212.72) * mm, "end": v(3.17, -212.72) * mm});
            skLineSegment(sketch, "E29.6.1.7", {"start": v(3.17, -187.33) * mm, "end": v(3.17, -212.72) * mm});
            skLineSegment(sketch, "E29.9.1.7", {"start": v(-3.18, -187.33) * mm, "end": v(3.17, -187.33) * mm});
            skLineSegment(sketch, "E29.0.1.8", {"start": v(-3.17, -254) * mm, "end": v(-3.17, -279.4) * mm});
            skLineSegment(sketch, "E29.3.1.8", {"start": v(-3.18, -279.4) * mm, "end": v(3.17, -279.4) * mm});
            skLineSegment(sketch, "E29.6.1.8", {"start": v(3.17, -254) * mm, "end": v(3.17, -279.4) * mm});
            skLineSegment(sketch, "E29.9.1.8", {"start": v(-3.18, -254) * mm, "end": v(3.17, -254) * mm});
            skLineSegment(sketch, "E29.0.2.7", {"start": v(249.93, -187.33) * mm, "end": v(249.93, -212.73) * mm});
            skLineSegment(sketch, "E29.3.2.7", {"start": v(249.93, -212.72) * mm, "end": v(256.28, -212.72) * mm});
            skLineSegment(sketch, "E29.6.2.7", {"start": v(256.28, -187.33) * mm, "end": v(256.28, -212.72) * mm});
            skLineSegment(sketch, "E29.9.2.7", {"start": v(249.93, -187.33) * mm, "end": v(256.28, -187.33) * mm});
            skLineSegment(sketch, "E29.0.2.8", {"start": v(249.93, -254) * mm, "end": v(249.93, -279.4) * mm});
            skLineSegment(sketch, "E29.3.2.8", {"start": v(249.93, -279.4) * mm, "end": v(256.28, -279.4) * mm});
            skLineSegment(sketch, "E29.6.2.8", {"start": v(256.28, -254) * mm, "end": v(256.28, -279.4) * mm});
            skLineSegment(sketch, "E29.9.2.8", {"start": v(249.93, -254) * mm, "end": v(256.28, -254) * mm});
            skLineSegment(sketch, "E30.bottom", {"start": v(-431.8, 171.91) * mm, "end": v(-406.4, 171.91) * mm});
            skLineSegment(sketch, "E30.top", {"start": v(-431.8, 165.56) * mm, "end": v(-406.4, 165.56) * mm});
            skLineSegment(sketch, "E30.left", {"start": v(-431.8, 171.91) * mm, "end": v(-431.8, 165.56) * mm});
            skLineSegment(sketch, "E30.right", {"start": v(-406.4, 171.91) * mm, "end": v(-406.4, 165.56) * mm});
            skLineSegment(sketch, "E31.0.1.0", {"start": v(-431.8, -3.17) * mm, "end": v(-406.4, -3.17) * mm});
            skLineSegment(sketch, "E31.0.1.1", {"start": v(-406.4, 3.18) * mm, "end": v(-406.4, -3.17) * mm});
            skLineSegment(sketch, "E31.0.1.2", {"start": v(-431.8, 3.18) * mm, "end": v(-406.4, 3.18) * mm});
            skLineSegment(sketch, "E31.0.1.3", {"start": v(-431.8, 3.18) * mm, "end": v(-431.8, -3.17) * mm});
            skLineSegment(sketch, "E31.0.2.0", {"start": v(-431.8, -171.91) * mm, "end": v(-406.4, -171.91) * mm});
            skLineSegment(sketch, "E31.0.2.1", {"start": v(-406.4, -165.56) * mm, "end": v(-406.4, -171.91) * mm});
            skLineSegment(sketch, "E31.0.2.2", {"start": v(-431.8, -165.56) * mm, "end": v(-406.4, -165.56) * mm});
            skLineSegment(sketch, "E31.0.2.3", {"start": v(-431.8, -165.56) * mm, "end": v(-431.8, -171.91) * mm});
            skLineSegment(sketch, "E31.1.0.0", {"start": v(-367.32, 165.56) * mm, "end": v(-341.92, 165.56) * mm});
            skLineSegment(sketch, "E31.1.0.1", {"start": v(-341.92, 171.91) * mm, "end": v(-341.92, 165.56) * mm});
            skLineSegment(sketch, "E31.1.0.2", {"start": v(-367.32, 171.91) * mm, "end": v(-341.92, 171.91) * mm});
            skLineSegment(sketch, "E31.1.0.3", {"start": v(-367.32, 171.91) * mm, "end": v(-367.32, 165.56) * mm});
            skLineSegment(sketch, "E31.1.1.0", {"start": v(-367.32, -3.17) * mm, "end": v(-341.92, -3.17) * mm});
            skLineSegment(sketch, "E31.1.1.1", {"start": v(-341.92, 3.18) * mm, "end": v(-341.92, -3.17) * mm});
            skLineSegment(sketch, "E31.1.1.2", {"start": v(-367.32, 3.18) * mm, "end": v(-341.92, 3.18) * mm});
            skLineSegment(sketch, "E31.1.1.3", {"start": v(-367.32, 3.18) * mm, "end": v(-367.32, -3.17) * mm});
            skLineSegment(sketch, "E31.1.2.0", {"start": v(-367.32, -171.91) * mm, "end": v(-341.92, -171.91) * mm});
            skLineSegment(sketch, "E31.1.2.1", {"start": v(-341.92, -165.56) * mm, "end": v(-341.92, -171.91) * mm});
            skLineSegment(sketch, "E31.1.2.2", {"start": v(-367.32, -165.56) * mm, "end": v(-341.92, -165.56) * mm});
            skLineSegment(sketch, "E31.1.2.3", {"start": v(-367.32, -165.56) * mm, "end": v(-367.32, -171.91) * mm});
            skLineSegment(sketch, "E31.2.0.0", {"start": v(-302.85, 165.56) * mm, "end": v(-277.45, 165.56) * mm});
            skLineSegment(sketch, "E31.2.0.1", {"start": v(-277.45, 171.91) * mm, "end": v(-277.45, 165.56) * mm});
            skLineSegment(sketch, "E31.2.0.2", {"start": v(-302.85, 171.91) * mm, "end": v(-277.45, 171.91) * mm});
            skLineSegment(sketch, "E31.2.0.3", {"start": v(-302.85, 171.91) * mm, "end": v(-302.85, 165.56) * mm});
            skLineSegment(sketch, "E31.2.1.0", {"start": v(-302.85, -3.17) * mm, "end": v(-277.45, -3.17) * mm});
            skLineSegment(sketch, "E31.2.1.1", {"start": v(-277.45, 3.18) * mm, "end": v(-277.45, -3.17) * mm});
            skLineSegment(sketch, "E31.2.1.2", {"start": v(-302.85, 3.18) * mm, "end": v(-277.45, 3.18) * mm});
            skLineSegment(sketch, "E31.2.1.3", {"start": v(-302.85, 3.18) * mm, "end": v(-302.85, -3.17) * mm});
            skLineSegment(sketch, "E31.2.2.0", {"start": v(-302.85, -171.91) * mm, "end": v(-277.45, -171.91) * mm});
            skLineSegment(sketch, "E31.2.2.1", {"start": v(-277.45, -165.56) * mm, "end": v(-277.45, -171.91) * mm});
            skLineSegment(sketch, "E31.2.2.2", {"start": v(-302.85, -165.56) * mm, "end": v(-277.45, -165.56) * mm});
            skLineSegment(sketch, "E31.2.2.3", {"start": v(-302.85, -165.56) * mm, "end": v(-302.85, -171.91) * mm});
            skLineSegment(sketch, "E31.3.0.0", {"start": v(-238.37, 165.56) * mm, "end": v(-212.97, 165.56) * mm});
            skLineSegment(sketch, "E31.3.0.1", {"start": v(-212.97, 171.91) * mm, "end": v(-212.97, 165.56) * mm});
            skLineSegment(sketch, "E31.3.0.2", {"start": v(-238.37, 171.91) * mm, "end": v(-212.97, 171.91) * mm});
            skLineSegment(sketch, "E31.3.0.3", {"start": v(-238.37, 171.91) * mm, "end": v(-238.37, 165.56) * mm});
            skLineSegment(sketch, "E31.3.1.0", {"start": v(-238.37, -3.17) * mm, "end": v(-212.97, -3.17) * mm});
            skLineSegment(sketch, "E31.3.1.1", {"start": v(-212.97, 3.18) * mm, "end": v(-212.97, -3.17) * mm});
            skLineSegment(sketch, "E31.3.1.2", {"start": v(-238.37, 3.18) * mm, "end": v(-212.97, 3.18) * mm});
            skLineSegment(sketch, "E31.3.1.3", {"start": v(-238.37, 3.18) * mm, "end": v(-238.37, -3.17) * mm});
            skLineSegment(sketch, "E31.3.2.0", {"start": v(-238.37, -171.91) * mm, "end": v(-212.97, -171.91) * mm});
            skLineSegment(sketch, "E31.3.2.1", {"start": v(-212.97, -165.56) * mm, "end": v(-212.97, -171.91) * mm});
            skLineSegment(sketch, "E31.3.2.2", {"start": v(-238.37, -165.56) * mm, "end": v(-212.97, -165.56) * mm});
            skLineSegment(sketch, "E31.3.2.3", {"start": v(-238.37, -165.56) * mm, "end": v(-238.37, -171.91) * mm});
            skLineSegment(sketch, "E31.4.0.0", {"start": v(-173.9, 165.56) * mm, "end": v(-148.5, 165.56) * mm});
            skLineSegment(sketch, "E31.4.0.1", {"start": v(-148.5, 171.91) * mm, "end": v(-148.5, 165.56) * mm});
            skLineSegment(sketch, "E31.4.0.2", {"start": v(-173.9, 171.91) * mm, "end": v(-148.5, 171.91) * mm});
            skLineSegment(sketch, "E31.4.0.3", {"start": v(-173.9, 171.91) * mm, "end": v(-173.9, 165.56) * mm});
            skLineSegment(sketch, "E31.4.1.0", {"start": v(-173.9, -3.17) * mm, "end": v(-148.5, -3.17) * mm});
            skLineSegment(sketch, "E31.4.1.1", {"start": v(-148.5, 3.18) * mm, "end": v(-148.5, -3.17) * mm});
            skLineSegment(sketch, "E31.4.1.2", {"start": v(-173.9, 3.18) * mm, "end": v(-148.5, 3.18) * mm});
            skLineSegment(sketch, "E31.4.1.3", {"start": v(-173.9, 3.18) * mm, "end": v(-173.9, -3.17) * mm});
            skLineSegment(sketch, "E31.4.2.0", {"start": v(-173.9, -171.91) * mm, "end": v(-148.5, -171.91) * mm});
            skLineSegment(sketch, "E31.4.2.1", {"start": v(-148.5, -165.56) * mm, "end": v(-148.5, -171.91) * mm});
            skLineSegment(sketch, "E31.4.2.2", {"start": v(-173.9, -165.56) * mm, "end": v(-148.5, -165.56) * mm});
            skLineSegment(sketch, "E31.4.2.3", {"start": v(-173.9, -165.56) * mm, "end": v(-173.9, -171.91) * mm});
            skLineSegment(sketch, "E31.5.0.0", {"start": v(-109.42, 165.56) * mm, "end": v(-84.02, 165.56) * mm});
            skLineSegment(sketch, "E31.5.0.1", {"start": v(-84.02, 171.91) * mm, "end": v(-84.02, 165.56) * mm});
            skLineSegment(sketch, "E31.5.0.2", {"start": v(-109.42, 171.91) * mm, "end": v(-84.02, 171.91) * mm});
            skLineSegment(sketch, "E31.5.0.3", {"start": v(-109.42, 171.91) * mm, "end": v(-109.42, 165.56) * mm});
            skLineSegment(sketch, "E31.5.1.0", {"start": v(-109.42, -3.17) * mm, "end": v(-84.02, -3.17) * mm});
            skLineSegment(sketch, "E31.5.1.1", {"start": v(-84.02, 3.18) * mm, "end": v(-84.02, -3.17) * mm});
            skLineSegment(sketch, "E31.5.1.2", {"start": v(-109.42, 3.18) * mm, "end": v(-84.02, 3.18) * mm});
            skLineSegment(sketch, "E31.5.1.3", {"start": v(-109.42, 3.18) * mm, "end": v(-109.42, -3.17) * mm});
            skLineSegment(sketch, "E31.5.2.0", {"start": v(-109.42, -171.91) * mm, "end": v(-84.02, -171.91) * mm});
            skLineSegment(sketch, "E31.5.2.1", {"start": v(-84.02, -165.56) * mm, "end": v(-84.02, -171.91) * mm});
            skLineSegment(sketch, "E31.5.2.2", {"start": v(-109.42, -165.56) * mm, "end": v(-84.02, -165.56) * mm});
            skLineSegment(sketch, "E31.5.2.3", {"start": v(-109.42, -165.56) * mm, "end": v(-109.42, -171.91) * mm});
            skLineSegment(sketch, "E31.6.0.0", {"start": v(-44.94, 165.56) * mm, "end": v(-19.54, 165.56) * mm});
            skLineSegment(sketch, "E31.6.0.1", {"start": v(-19.54, 171.91) * mm, "end": v(-19.54, 165.56) * mm});
            skLineSegment(sketch, "E31.6.0.2", {"start": v(-44.94, 171.91) * mm, "end": v(-19.54, 171.91) * mm});
            skLineSegment(sketch, "E31.6.0.3", {"start": v(-44.94, 171.91) * mm, "end": v(-44.94, 165.56) * mm});
            skLineSegment(sketch, "E31.6.1.0", {"start": v(-44.94, -3.17) * mm, "end": v(-19.54, -3.17) * mm});
            skLineSegment(sketch, "E31.6.1.1", {"start": v(-19.54, 3.18) * mm, "end": v(-19.54, -3.17) * mm});
            skLineSegment(sketch, "E31.6.1.2", {"start": v(-44.94, 3.18) * mm, "end": v(-19.54, 3.18) * mm});
            skLineSegment(sketch, "E31.6.1.3", {"start": v(-44.94, 3.18) * mm, "end": v(-44.94, -3.17) * mm});
            skLineSegment(sketch, "E31.6.2.0", {"start": v(-44.94, -171.91) * mm, "end": v(-19.54, -171.91) * mm});
            skLineSegment(sketch, "E31.6.2.1", {"start": v(-19.54, -165.56) * mm, "end": v(-19.54, -171.91) * mm});
            skLineSegment(sketch, "E31.6.2.2", {"start": v(-44.94, -165.56) * mm, "end": v(-19.54, -165.56) * mm});
            skLineSegment(sketch, "E31.6.2.3", {"start": v(-44.94, -165.56) * mm, "end": v(-44.94, -171.91) * mm});
            skLineSegment(sketch, "E31.7.0.0", {"start": v(19.54, 165.56) * mm, "end": v(44.94, 165.56) * mm});
            skLineSegment(sketch, "E31.7.0.1", {"start": v(44.94, 171.91) * mm, "end": v(44.94, 165.56) * mm});
            skLineSegment(sketch, "E31.7.0.2", {"start": v(19.54, 171.91) * mm, "end": v(44.94, 171.91) * mm});
            skLineSegment(sketch, "E31.7.0.3", {"start": v(19.54, 171.91) * mm, "end": v(19.54, 165.56) * mm});
            skLineSegment(sketch, "E31.7.1.0", {"start": v(19.54, -3.17) * mm, "end": v(44.94, -3.17) * mm});
            skLineSegment(sketch, "E31.7.1.1", {"start": v(44.94, 3.18) * mm, "end": v(44.94, -3.17) * mm});
            skLineSegment(sketch, "E31.7.1.2", {"start": v(19.54, 3.18) * mm, "end": v(44.94, 3.18) * mm});
            skLineSegment(sketch, "E31.7.1.3", {"start": v(19.54, 3.18) * mm, "end": v(19.54, -3.17) * mm});
            skLineSegment(sketch, "E31.7.2.0", {"start": v(19.54, -171.91) * mm, "end": v(44.94, -171.91) * mm});
            skLineSegment(sketch, "E31.7.2.1", {"start": v(44.94, -165.56) * mm, "end": v(44.94, -171.91) * mm});
            skLineSegment(sketch, "E31.7.2.2", {"start": v(19.54, -165.56) * mm, "end": v(44.94, -165.56) * mm});
            skLineSegment(sketch, "E31.7.2.3", {"start": v(19.54, -165.56) * mm, "end": v(19.54, -171.91) * mm});
            skLineSegment(sketch, "E31.8.0.0", {"start": v(84.02, 165.56) * mm, "end": v(109.42, 165.56) * mm});
            skLineSegment(sketch, "E31.8.0.1", {"start": v(109.42, 171.91) * mm, "end": v(109.42, 165.56) * mm});
            skLineSegment(sketch, "E31.8.0.2", {"start": v(84.02, 171.91) * mm, "end": v(109.42, 171.91) * mm});
            skLineSegment(sketch, "E31.8.0.3", {"start": v(84.02, 171.91) * mm, "end": v(84.02, 165.56) * mm});
            skLineSegment(sketch, "E31.8.1.0", {"start": v(84.02, -3.17) * mm, "end": v(109.42, -3.17) * mm});
            skLineSegment(sketch, "E31.8.1.1", {"start": v(109.42, 3.18) * mm, "end": v(109.42, -3.17) * mm});
            skLineSegment(sketch, "E31.8.1.2", {"start": v(84.02, 3.18) * mm, "end": v(109.42, 3.18) * mm});
            skLineSegment(sketch, "E31.8.1.3", {"start": v(84.02, 3.18) * mm, "end": v(84.02, -3.17) * mm});
            skLineSegment(sketch, "E31.8.2.0", {"start": v(84.02, -171.91) * mm, "end": v(109.42, -171.91) * mm});
            skLineSegment(sketch, "E31.8.2.1", {"start": v(109.42, -165.56) * mm, "end": v(109.42, -171.91) * mm});
            skLineSegment(sketch, "E31.8.2.2", {"start": v(84.02, -165.56) * mm, "end": v(109.42, -165.56) * mm});
            skLineSegment(sketch, "E31.8.2.3", {"start": v(84.02, -165.56) * mm, "end": v(84.02, -171.91) * mm});
            skLineSegment(sketch, "E31.9.0.0", {"start": v(148.5, 165.56) * mm, "end": v(173.9, 165.56) * mm});
            skLineSegment(sketch, "E31.9.0.1", {"start": v(173.9, 171.91) * mm, "end": v(173.9, 165.56) * mm});
            skLineSegment(sketch, "E31.9.0.2", {"start": v(148.5, 171.91) * mm, "end": v(173.9, 171.91) * mm});
            skLineSegment(sketch, "E31.9.0.3", {"start": v(148.5, 171.91) * mm, "end": v(148.5, 165.56) * mm});
            skLineSegment(sketch, "E31.9.1.0", {"start": v(148.5, -3.17) * mm, "end": v(173.9, -3.17) * mm});
            skLineSegment(sketch, "E31.9.1.1", {"start": v(173.9, 3.18) * mm, "end": v(173.9, -3.17) * mm});
            skLineSegment(sketch, "E31.9.1.2", {"start": v(148.5, 3.18) * mm, "end": v(173.9, 3.18) * mm});
            skLineSegment(sketch, "E31.9.1.3", {"start": v(148.5, 3.18) * mm, "end": v(148.5, -3.17) * mm});
            skLineSegment(sketch, "E31.9.2.0", {"start": v(148.5, -171.91) * mm, "end": v(173.9, -171.91) * mm});
            skLineSegment(sketch, "E31.9.2.1", {"start": v(173.9, -165.56) * mm, "end": v(173.9, -171.91) * mm});
            skLineSegment(sketch, "E31.9.2.2", {"start": v(148.5, -165.56) * mm, "end": v(173.9, -165.56) * mm});
            skLineSegment(sketch, "E31.9.2.3", {"start": v(148.5, -165.56) * mm, "end": v(148.5, -171.91) * mm});
            skLineSegment(sketch, "E31.10.0.0", {"start": v(212.97, 165.56) * mm, "end": v(238.37, 165.56) * mm});
            skLineSegment(sketch, "E31.10.0.1", {"start": v(238.37, 171.91) * mm, "end": v(238.37, 165.56) * mm});
            skLineSegment(sketch, "E31.10.0.2", {"start": v(212.97, 171.91) * mm, "end": v(238.37, 171.91) * mm});
            skLineSegment(sketch, "E31.10.0.3", {"start": v(212.97, 171.91) * mm, "end": v(212.97, 165.56) * mm});
            skLineSegment(sketch, "E31.10.1.0", {"start": v(212.97, -3.17) * mm, "end": v(238.37, -3.17) * mm});
            skLineSegment(sketch, "E31.10.1.1", {"start": v(238.37, 3.18) * mm, "end": v(238.37, -3.17) * mm});
            skLineSegment(sketch, "E31.10.1.2", {"start": v(212.97, 3.18) * mm, "end": v(238.37, 3.18) * mm});
            skLineSegment(sketch, "E31.10.1.3", {"start": v(212.97, 3.18) * mm, "end": v(212.97, -3.17) * mm});
            skLineSegment(sketch, "E31.10.2.0", {"start": v(212.97, -171.91) * mm, "end": v(238.37, -171.91) * mm});
            skLineSegment(sketch, "E31.10.2.1", {"start": v(238.37, -165.56) * mm, "end": v(238.37, -171.91) * mm});
            skLineSegment(sketch, "E31.10.2.2", {"start": v(212.97, -165.56) * mm, "end": v(238.37, -165.56) * mm});
            skLineSegment(sketch, "E31.10.2.3", {"start": v(212.97, -165.56) * mm, "end": v(212.97, -171.91) * mm});
            skLineSegment(sketch, "E31.11.0.0", {"start": v(277.45, 165.56) * mm, "end": v(302.85, 165.56) * mm});
            skLineSegment(sketch, "E31.11.0.1", {"start": v(302.85, 171.91) * mm, "end": v(302.85, 165.56) * mm});
            skLineSegment(sketch, "E31.11.0.2", {"start": v(277.45, 171.91) * mm, "end": v(302.85, 171.91) * mm});
            skLineSegment(sketch, "E31.11.0.3", {"start": v(277.45, 171.91) * mm, "end": v(277.45, 165.56) * mm});
            skLineSegment(sketch, "E31.11.1.0", {"start": v(277.45, -3.17) * mm, "end": v(302.85, -3.17) * mm});
            skLineSegment(sketch, "E31.11.1.1", {"start": v(302.85, 3.18) * mm, "end": v(302.85, -3.17) * mm});
            skLineSegment(sketch, "E31.11.1.2", {"start": v(277.45, 3.18) * mm, "end": v(302.85, 3.18) * mm});
            skLineSegment(sketch, "E31.11.1.3", {"start": v(277.45, 3.18) * mm, "end": v(277.45, -3.17) * mm});
            skLineSegment(sketch, "E31.11.2.0", {"start": v(277.45, -171.91) * mm, "end": v(302.85, -171.91) * mm});
            skLineSegment(sketch, "E31.11.2.1", {"start": v(302.85, -165.56) * mm, "end": v(302.85, -171.91) * mm});
            skLineSegment(sketch, "E31.11.2.2", {"start": v(277.45, -165.56) * mm, "end": v(302.85, -165.56) * mm});
            skLineSegment(sketch, "E31.11.2.3", {"start": v(277.45, -165.56) * mm, "end": v(277.45, -171.91) * mm});
            skLineSegment(sketch, "E31.12.0.0", {"start": v(341.92, 165.56) * mm, "end": v(367.32, 165.56) * mm});
            skLineSegment(sketch, "E31.12.0.1", {"start": v(367.32, 171.91) * mm, "end": v(367.32, 165.56) * mm});
            skLineSegment(sketch, "E31.12.0.2", {"start": v(341.92, 171.91) * mm, "end": v(367.32, 171.91) * mm});
            skLineSegment(sketch, "E31.12.0.3", {"start": v(341.92, 171.91) * mm, "end": v(341.92, 165.56) * mm});
            skLineSegment(sketch, "E31.12.1.0", {"start": v(341.92, -3.17) * mm, "end": v(367.32, -3.17) * mm});
            skLineSegment(sketch, "E31.12.1.1", {"start": v(367.32, 3.18) * mm, "end": v(367.32, -3.17) * mm});
            skLineSegment(sketch, "E31.12.1.2", {"start": v(341.92, 3.18) * mm, "end": v(367.32, 3.18) * mm});
            skLineSegment(sketch, "E31.12.1.3", {"start": v(341.92, 3.18) * mm, "end": v(341.92, -3.17) * mm});
            skLineSegment(sketch, "E31.12.2.0", {"start": v(341.92, -171.91) * mm, "end": v(367.32, -171.91) * mm});
            skLineSegment(sketch, "E31.12.2.1", {"start": v(367.32, -165.56) * mm, "end": v(367.32, -171.91) * mm});
            skLineSegment(sketch, "E31.12.2.2", {"start": v(341.92, -165.56) * mm, "end": v(367.32, -165.56) * mm});
            skLineSegment(sketch, "E31.12.2.3", {"start": v(341.92, -165.56) * mm, "end": v(341.92, -171.91) * mm});
            skLineSegment(sketch, "E31.13.0.0", {"start": v(406.4, 165.56) * mm, "end": v(431.8, 165.56) * mm});
            skLineSegment(sketch, "E31.13.0.1", {"start": v(431.8, 171.91) * mm, "end": v(431.8, 165.56) * mm});
            skLineSegment(sketch, "E31.13.0.2", {"start": v(406.4, 171.91) * mm, "end": v(431.8, 171.91) * mm});
            skLineSegment(sketch, "E31.13.0.3", {"start": v(406.4, 171.91) * mm, "end": v(406.4, 165.56) * mm});
            skLineSegment(sketch, "E31.13.1.0", {"start": v(406.4, -3.17) * mm, "end": v(431.8, -3.17) * mm});
            skLineSegment(sketch, "E31.13.1.1", {"start": v(431.8, 3.18) * mm, "end": v(431.8, -3.17) * mm});
            skLineSegment(sketch, "E31.13.1.2", {"start": v(406.4, 3.18) * mm, "end": v(431.8, 3.18) * mm});
            skLineSegment(sketch, "E31.13.1.3", {"start": v(406.4, 3.18) * mm, "end": v(406.4, -3.17) * mm});
            skLineSegment(sketch, "E31.13.2.0", {"start": v(406.4, -171.91) * mm, "end": v(431.8, -171.91) * mm});
            skLineSegment(sketch, "E31.13.2.1", {"start": v(431.8, -165.56) * mm, "end": v(431.8, -171.91) * mm});
            skLineSegment(sketch, "E31.13.2.2", {"start": v(406.4, -165.56) * mm, "end": v(431.8, -165.56) * mm});
            skLineSegment(sketch, "E31.13.2.3", {"start": v(406.4, -165.56) * mm, "end": v(406.4, -171.91) * mm});
            skLineSegment(sketch, "E31.direction1", {"start": v(-431.8, 165.56) * mm, "end": v(-367.32, 165.56) * mm, "construction": true});
            skLineSegment(sketch, "E31.direction2", {"start": v(-431.8, 165.56) * mm, "end": v(-431.8, -3.17) * mm, "construction": true});
            skSolve(sketch);
        }
        {
            var Q0;
            Q0 = qSketchRegion(id + "F5", true);
            extrude(context, id + "F7", {"entities" : qUnion([Q0]), "oppositeDirection" : true, "depth" : (getVariable(context, 'thick')) * mm, "offsetDistance" : 25.4 * mm});
        }
        {
            var Q0;
            Q0 = qSketchRegion(id + "F5", true);
            extrude(context, id + "F8", {"entities" : qUnion([Q0]), "oppositeDirection" : true, "depth" : (getVariable(context, 'height')) * mm, "offsetDistance" : 25.4 * mm, "hasSecondDirection" : true, "secondDirectionOppositeDirection" : true, "secondDirectionDepth" : ((getVariable(context, 'height')) - (getVariable(context, 'thick'))) * mm});
        }
        {
            var Q0;
            Q0 = qSketchRegion(id + "F6", true);
            extrude(context, id + "F9", {"entities" : qUnion([Q0]), "operationType" : NewBodyOperationType.REMOVE, "endBound" : BoundingType.THROUGH_ALL, "oppositeDirection" : true, "depth" : 25.4 * mm, "offsetDistance" : 25.4 * mm});
        }
        {
            var Q0;
            Q0 = qSketchRegion(id + "F4", true);
            extrude(context, id + "F10", {"entities" : qUnion([Q0]), "oppositeDirection" : true, "depth" : (getVariable(context, 'height')) * mm, "offsetDistance" : 25.4 * mm});
        }
        {
            var Q0;
            Q0 = qSketchRegion(id + "F3", true);
            extrude(context, id + "F11", {"entities" : qUnion([Q0]), "operationType" : NewBodyOperationType.REMOVE, "oppositeDirection" : true, "depth" : ((getVariable(context, 'height')) / 2) * mm, "offsetDistance" : 25.4 * mm});
        }
        {
            var Q0;
            Q0 = qSketchRegion(id + "F3", true);
            extrude(context, id + "F12", {"entities" : qUnion([Q0]), "oppositeDirection" : true, "depth" : (getVariable(context, 'height')) * mm, "offsetDistance" : 25.4 * mm});
        }
        {
            var Q0;
            Q0=makeQuery(id+"F10.opExtrude","SWEPT_BODY",BODY,{"disambiguationData":[OSD([sQuery(id+"F4.wireOp",EDGE,"E13.bottom"),sQuery(id+"F4.wireOp",EDGE,"E13.top"),sQuery(id+"F4.wireOp",EDGE,"E13.left"),sQuery(id+"F4.wireOp",EDGE,"E13.right")])]});
            var Q1;
            Q1=makeQuery(id+"F10.opExtrude","SWEPT_BODY",BODY,{"disambiguationData":[OSD([sQuery(id+"F4.wireOp",EDGE,"E14.bottom"),sQuery(id+"F4.wireOp",EDGE,"E14.top"),sQuery(id+"F4.wireOp",EDGE,"E14.left"),sQuery(id+"F4.wireOp",EDGE,"E14.right")])]});
            var Q2;
            Q2=makeQuery(id+"F10.opExtrude","SWEPT_BODY",BODY,{"disambiguationData":[OSD([sQuery(id+"F4.wireOp",EDGE,"E15.bottom"),sQuery(id+"F4.wireOp",EDGE,"E15.top"),sQuery(id+"F4.wireOp",EDGE,"E15.left"),sQuery(id+"F4.wireOp",EDGE,"E15.right")])]});
            var Q3;
            Q3=makeQuery(id+"F10.opExtrude","SWEPT_BODY",BODY,{"disambiguationData":[OSD([sQuery(id+"F4.wireOp",EDGE,"E16.bottom"),sQuery(id+"F4.wireOp",EDGE,"E16.top"),sQuery(id+"F4.wireOp",EDGE,"E16.left"),sQuery(id+"F4.wireOp",EDGE,"E16.right")])]});
            var Q4;
            Q4=makeQuery(id+"F10.opExtrude","SWEPT_BODY",BODY,{"disambiguationData":[OSD([sQuery(id+"F4.wireOp",EDGE,"E17.bottom"),sQuery(id+"F4.wireOp",EDGE,"E17.top"),sQuery(id+"F4.wireOp",EDGE,"E17.left"),sQuery(id+"F4.wireOp",EDGE,"E17.right")])]});
            var Q5;
            Q5=makeQuery(id+"F12.opExtrude","SWEPT_BODY",BODY,{"disambiguationData":[OSD([sQuery(id+"F3.wireOp",EDGE,"E8.bottom"),sQuery(id+"F3.wireOp",EDGE,"E8.top"),sQuery(id+"F3.wireOp",EDGE,"E8.left"),sQuery(id+"F3.wireOp",EDGE,"E8.right")])]});
            var Q6;
            Q6=makeQuery(id+"F12.opExtrude","SWEPT_BODY",BODY,{"disambiguationData":[OSD([sQuery(id+"F3.wireOp",EDGE,"E9.bottom"),sQuery(id+"F3.wireOp",EDGE,"E9.top"),sQuery(id+"F3.wireOp",EDGE,"E9.left"),sQuery(id+"F3.wireOp",EDGE,"E9.right")])]});
            var Q7;
            Q7=makeQuery(id+"F12.opExtrude","SWEPT_BODY",BODY,{"disambiguationData":[OSD([sQuery(id+"F3.wireOp",EDGE,"E11.bottom"),sQuery(id+"F3.wireOp",EDGE,"E11.top"),sQuery(id+"F3.wireOp",EDGE,"E11.left"),sQuery(id+"F3.wireOp",EDGE,"E11.right")])]});
            var Q8;
            Q8=makeQuery(id+"F12.opExtrude","SWEPT_BODY",BODY,{"disambiguationData":[OSD([sQuery(id+"F3.wireOp",EDGE,"E10.bottom"),sQuery(id+"F3.wireOp",EDGE,"E10.top"),sQuery(id+"F3.wireOp",EDGE,"E10.left"),sQuery(id+"F3.wireOp",EDGE,"E10.right")])]});
            var Q9;
            Q9=makeQuery(id+"F12.opExtrude","SWEPT_BODY",BODY,{"disambiguationData":[OSD([sQuery(id+"F3.wireOp",EDGE,"E12.bottom"),sQuery(id+"F3.wireOp",EDGE,"E12.top"),sQuery(id+"F3.wireOp",EDGE,"E12.left"),sQuery(id+"F3.wireOp",EDGE,"E12.right")])]});
            booleanBodies(context, id + "F13", {"operationType" : BooleanOperationType.SUBTRACTION, "tools" : qUnion([Q0, Q1, Q2, Q3, Q4]), "targets" : qUnion([Q5, Q6, Q7, Q8, Q9]), "keepTools" : true});
        }
        {
            var Q0;
            Q0=makeQuery(id+"F7.opExtrude","SWEPT_BODY",BODY,{"disambiguationData":[OSD([sQuery(id+"F5.wireOp",EDGE,"E18.bottom"),sQuery(id+"F5.wireOp",EDGE,"E18.top"),sQuery(id+"F5.wireOp",EDGE,"E18.left"),sQuery(id+"F5.wireOp",EDGE,"E18.right"),sQuery(id+"F5.wireOp",EDGE,"E19.bottom"),sQuery(id+"F5.wireOp",EDGE,"E19.top"),sQuery(id+"F5.wireOp",EDGE,"E19.left"),sQuery(id+"F5.wireOp",EDGE,"E19.right"),sQuery(id+"F5.wireOp",EDGE,"E20.1.0.0"),sQuery(id+"F5.wireOp",EDGE,"E20.1.0.1"),sQuery(id+"F5.wireOp",EDGE,"E20.1.0.2"),sQuery(id+"F5.wireOp",EDGE,"E20.2.0.0"),sQuery(id+"F5.wireOp",EDGE,"E20.2.0.1"),sQuery(id+"F5.wireOp",EDGE,"E20.2.0.2"),sQuery(id+"F5.wireOp",EDGE,"E20.3.0.0"),sQuery(id+"F5.wireOp",EDGE,"E20.3.0.1"),sQuery(id+"F5.wireOp",EDGE,"E20.3.0.2"),sQuery(id+"F5.wireOp",EDGE,"E20.4.0.0"),sQuery(id+"F5.wireOp",EDGE,"E20.4.0.1"),sQuery(id+"F5.wireOp",EDGE,"E20.4.0.2"),sQuery(id+"F5.wireOp",EDGE,"E20.5.0.0"),sQuery(id+"F5.wireOp",EDGE,"E20.5.0.1"),sQuery(id+"F5.wireOp",EDGE,"E20.5.0.2"),sQuery(id+"F5.wireOp",EDGE,"E20.6.0.0"),sQuery(id+"F5.wireOp",EDGE,"E20.6.0.1"),sQuery(id+"F5.wireOp",EDGE,"E20.6.0.2"),sQuery(id+"F5.wireOp",EDGE,"E20.7.0.0"),sQuery(id+"F5.wireOp",EDGE,"E20.7.0.1"),sQuery(id+"F5.wireOp",EDGE,"E20.7.0.2"),sQuery(id+"F5.wireOp",EDGE,"E20.8.0.0"),sQuery(id+"F5.wireOp",EDGE,"E20.8.0.1"),sQuery(id+"F5.wireOp",EDGE,"E20.8.0.2"),sQuery(id+"F5.wireOp",EDGE,"E20.9.0.0"),sQuery(id+"F5.wireOp",EDGE,"E20.9.0.1"),sQuery(id+"F5.wireOp",EDGE,"E20.9.0.2"),sQuery(id+"F5.wireOp",EDGE,"E20.10.0.0"),sQuery(id+"F5.wireOp",EDGE,"E20.10.0.1"),sQuery(id+"F5.wireOp",EDGE,"E20.10.0.2"),sQuery(id+"F5.wireOp",EDGE,"E20.11.0.0"),sQuery(id+"F5.wireOp",EDGE,"E20.11.0.1"),sQuery(id+"F5.wireOp",EDGE,"E20.11.0.2"),sQuery(id+"F5.wireOp",EDGE,"E20.12.0.0"),sQuery(id+"F5.wireOp",EDGE,"E20.12.0.1"),sQuery(id+"F5.wireOp",EDGE,"E20.12.0.2"),sQuery(id+"F5.wireOp",EDGE,"E20.13.0.0"),sQuery(id+"F5.wireOp",EDGE,"E20.13.0.1"),sQuery(id+"F5.wireOp",EDGE,"E20.13.0.2"),sQuery(id+"F5.wireOp",EDGE,"E20.14.0.0"),sQuery(id+"F5.wireOp",EDGE,"E20.14.0.1"),sQuery(id+"F5.wireOp",EDGE,"E20.14.0.2"),sQuery(id+"F5.wireOp",EDGE,"E20.15.0.0"),sQuery(id+"F5.wireOp",EDGE,"E20.15.0.1"),sQuery(id+"F5.wireOp",EDGE,"E20.15.0.2"),sQuery(id+"F5.wireOp",EDGE,"E20.16.0.0"),sQuery(id+"F5.wireOp",EDGE,"E20.16.0.1"),sQuery(id+"F5.wireOp",EDGE,"E20.16.0.2"),sQuery(id+"F5.wireOp",EDGE,"E20.17.0.0"),sQuery(id+"F5.wireOp",EDGE,"E20.17.0.1"),sQuery(id+"F5.wireOp",EDGE,"E20.17.0.2"),sQuery(id+"F5.wireOp",EDGE,"E21.bottom"),sQuery(id+"F5.wireOp",EDGE,"E21.top"),sQuery(id+"F5.wireOp",EDGE,"E21.left"),sQuery(id+"F5.wireOp",EDGE,"E21.right"),sQuery(id+"F5.wireOp",EDGE,"E22.0.1.0"),sQuery(id+"F5.wireOp",EDGE,"E22.0.1.1"),sQuery(id+"F5.wireOp",EDGE,"E22.0.1.2"),sQuery(id+"F5.wireOp",EDGE,"E22.0.2.0"),sQuery(id+"F5.wireOp",EDGE,"E22.0.2.1"),sQuery(id+"F5.wireOp",EDGE,"E22.0.2.2"),sQuery(id+"F5.wireOp",EDGE,"E22.0.3.0"),sQuery(id+"F5.wireOp",EDGE,"E22.0.3.1"),sQuery(id+"F5.wireOp",EDGE,"E22.0.3.2"),sQuery(id+"F5.wireOp",EDGE,"E22.0.4.0"),sQuery(id+"F5.wireOp",EDGE,"E22.0.4.1"),sQuery(id+"F5.wireOp",EDGE,"E22.0.4.2"),sQuery(id+"F5.wireOp",EDGE,"E22.0.5.0"),sQuery(id+"F5.wireOp",EDGE,"E22.0.5.1"),sQuery(id+"F5.wireOp",EDGE,"E22.0.5.2"),sQuery(id+"F5.wireOp",EDGE,"E22.0.6.0"),sQuery(id+"F5.wireOp",EDGE,"E22.0.6.1"),sQuery(id+"F5.wireOp",EDGE,"E22.0.6.2"),sQuery(id+"F5.wireOp",EDGE,"E22.0.7.0"),sQuery(id+"F5.wireOp",EDGE,"E22.0.7.1"),sQuery(id+"F5.wireOp",EDGE,"E22.0.7.2"),sQuery(id+"F5.wireOp",EDGE,"E22.0.8.0"),sQuery(id+"F5.wireOp",EDGE,"E22.0.8.1"),sQuery(id+"F5.wireOp",EDGE,"E22.0.8.2"),sQuery(id+"F5.wireOp",EDGE,"E22.0.9.0"),sQuery(id+"F5.wireOp",EDGE,"E22.0.9.1"),sQuery(id+"F5.wireOp",EDGE,"E22.0.9.2"),sQuery(id+"F5.wireOp",EDGE,"E22.0.10.0"),sQuery(id+"F5.wireOp",EDGE,"E22.0.10.1"),sQuery(id+"F5.wireOp",EDGE,"E22.0.10.2"),sQuery(id+"F5.wireOp",EDGE,"E22.0.11.0"),sQuery(id+"F5.wireOp",EDGE,"E22.0.11.1"),sQuery(id+"F5.wireOp",EDGE,"E22.0.11.2"),sQuery(id+"F5.wireOp",EDGE,"E23.bottom"),sQuery(id+"F5.wireOp",EDGE,"E23.top"),sQuery(id+"F5.wireOp",EDGE,"E23.left"),sQuery(id+"F5.wireOp",EDGE,"E23.right"),sQuery(id+"F5.wireOp",EDGE,"E24.1.0.0"),sQuery(id+"F5.wireOp",EDGE,"E24.1.0.1"),sQuery(id+"F5.wireOp",EDGE,"E24.1.0.3"),sQuery(id+"F5.wireOp",EDGE,"E24.2.0.0"),sQuery(id+"F5.wireOp",EDGE,"E24.2.0.1"),sQuery(id+"F5.wireOp",EDGE,"E24.2.0.3"),sQuery(id+"F5.wireOp",EDGE,"E24.3.0.0"),sQuery(id+"F5.wireOp",EDGE,"E24.3.0.1"),sQuery(id+"F5.wireOp",EDGE,"E24.3.0.3"),sQuery(id+"F5.wireOp",EDGE,"E24.4.0.0"),sQuery(id+"F5.wireOp",EDGE,"E24.4.0.1"),sQuery(id+"F5.wireOp",EDGE,"E24.4.0.3"),sQuery(id+"F5.wireOp",EDGE,"E24.5.0.0"),sQuery(id+"F5.wireOp",EDGE,"E24.5.0.1"),sQuery(id+"F5.wireOp",EDGE,"E24.5.0.3"),sQuery(id+"F5.wireOp",EDGE,"E24.6.0.0"),sQuery(id+"F5.wireOp",EDGE,"E24.6.0.1"),sQuery(id+"F5.wireOp",EDGE,"E24.6.0.3"),sQuery(id+"F5.wireOp",EDGE,"E24.7.0.0"),sQuery(id+"F5.wireOp",EDGE,"E24.7.0.1"),sQuery(id+"F5.wireOp",EDGE,"E24.7.0.3"),sQuery(id+"F5.wireOp",EDGE,"E24.8.0.0"),sQuery(id+"F5.wireOp",EDGE,"E24.8.0.1"),sQuery(id+"F5.wireOp",EDGE,"E24.8.0.3"),sQuery(id+"F5.wireOp",EDGE,"E24.9.0.0"),sQuery(id+"F5.wireOp",EDGE,"E24.9.0.1"),sQuery(id+"F5.wireOp",EDGE,"E24.9.0.3"),sQuery(id+"F5.wireOp",EDGE,"E24.10.0.0"),sQuery(id+"F5.wireOp",EDGE,"E24.10.0.1"),sQuery(id+"F5.wireOp",EDGE,"E24.10.0.3"),sQuery(id+"F5.wireOp",EDGE,"E24.11.0.0"),sQuery(id+"F5.wireOp",EDGE,"E24.11.0.1"),sQuery(id+"F5.wireOp",EDGE,"E24.11.0.3"),sQuery(id+"F5.wireOp",EDGE,"E24.12.0.0"),sQuery(id+"F5.wireOp",EDGE,"E24.12.0.1"),sQuery(id+"F5.wireOp",EDGE,"E24.12.0.3"),sQuery(id+"F5.wireOp",EDGE,"E24.13.0.0"),sQuery(id+"F5.wireOp",EDGE,"E24.13.0.1"),sQuery(id+"F5.wireOp",EDGE,"E24.13.0.3"),sQuery(id+"F5.wireOp",EDGE,"E24.14.0.0"),sQuery(id+"F5.wireOp",EDGE,"E24.14.0.1"),sQuery(id+"F5.wireOp",EDGE,"E24.14.0.3"),sQuery(id+"F5.wireOp",EDGE,"E24.15.0.0"),sQuery(id+"F5.wireOp",EDGE,"E24.15.0.1"),sQuery(id+"F5.wireOp",EDGE,"E24.15.0.3"),sQuery(id+"F5.wireOp",EDGE,"E24.16.0.0"),sQuery(id+"F5.wireOp",EDGE,"E24.16.0.1"),sQuery(id+"F5.wireOp",EDGE,"E24.16.0.3"),sQuery(id+"F5.wireOp",EDGE,"E24.17.0.0"),sQuery(id+"F5.wireOp",EDGE,"E24.17.0.1"),sQuery(id+"F5.wireOp",EDGE,"E24.17.0.3"),sQuery(id+"F5.wireOp",EDGE,"E25.bottom"),sQuery(id+"F5.wireOp",EDGE,"E25.top"),sQuery(id+"F5.wireOp",EDGE,"E25.left"),sQuery(id+"F5.wireOp",EDGE,"E25.right"),sQuery(id+"F5.wireOp",EDGE,"E26.0.1.1"),sQuery(id+"F5.wireOp",EDGE,"E26.0.1.2"),sQuery(id+"F5.wireOp",EDGE,"E26.0.1.3"),sQuery(id+"F5.wireOp",EDGE,"E26.0.2.1"),sQuery(id+"F5.wireOp",EDGE,"E26.0.2.2"),sQuery(id+"F5.wireOp",EDGE,"E26.0.2.3"),sQuery(id+"F5.wireOp",EDGE,"E26.0.3.1"),sQuery(id+"F5.wireOp",EDGE,"E26.0.3.2"),sQuery(id+"F5.wireOp",EDGE,"E26.0.3.3"),sQuery(id+"F5.wireOp",EDGE,"E26.0.4.1"),sQuery(id+"F5.wireOp",EDGE,"E26.0.4.2"),sQuery(id+"F5.wireOp",EDGE,"E26.0.4.3"),sQuery(id+"F5.wireOp",EDGE,"E26.0.5.1"),sQuery(id+"F5.wireOp",EDGE,"E26.0.5.2"),sQuery(id+"F5.wireOp",EDGE,"E26.0.5.3"),sQuery(id+"F5.wireOp",EDGE,"E26.0.6.1"),sQuery(id+"F5.wireOp",EDGE,"E26.0.6.2"),sQuery(id+"F5.wireOp",EDGE,"E26.0.6.3"),sQuery(id+"F5.wireOp",EDGE,"E26.0.7.1"),sQuery(id+"F5.wireOp",EDGE,"E26.0.7.2"),sQuery(id+"F5.wireOp",EDGE,"E26.0.7.3"),sQuery(id+"F5.wireOp",EDGE,"E26.0.8.1"),sQuery(id+"F5.wireOp",EDGE,"E26.0.8.2"),sQuery(id+"F5.wireOp",EDGE,"E26.0.8.3"),sQuery(id+"F5.wireOp",EDGE,"E26.0.9.1"),sQuery(id+"F5.wireOp",EDGE,"E26.0.9.2"),sQuery(id+"F5.wireOp",EDGE,"E26.0.9.3"),sQuery(id+"F5.wireOp",EDGE,"E26.0.10.1"),sQuery(id+"F5.wireOp",EDGE,"E26.0.10.2"),sQuery(id+"F5.wireOp",EDGE,"E26.0.10.3"),sQuery(id+"F5.wireOp",EDGE,"E26.0.11.1"),sQuery(id+"F5.wireOp",EDGE,"E26.0.11.2"),sQuery(id+"F5.wireOp",EDGE,"E26.0.11.3")])]});
            var Q1;
            Q1=makeQuery(id+"F8.opExtrude","SWEPT_BODY",BODY,{"disambiguationData":[OSD([sQuery(id+"F5.wireOp",EDGE,"E18.bottom"),sQuery(id+"F5.wireOp",EDGE,"E18.top"),sQuery(id+"F5.wireOp",EDGE,"E18.left"),sQuery(id+"F5.wireOp",EDGE,"E18.right"),sQuery(id+"F5.wireOp",EDGE,"E19.bottom"),sQuery(id+"F5.wireOp",EDGE,"E19.top"),sQuery(id+"F5.wireOp",EDGE,"E19.left"),sQuery(id+"F5.wireOp",EDGE,"E19.right"),sQuery(id+"F5.wireOp",EDGE,"E20.1.0.0"),sQuery(id+"F5.wireOp",EDGE,"E20.1.0.1"),sQuery(id+"F5.wireOp",EDGE,"E20.1.0.2"),sQuery(id+"F5.wireOp",EDGE,"E20.2.0.0"),sQuery(id+"F5.wireOp",EDGE,"E20.2.0.1"),sQuery(id+"F5.wireOp",EDGE,"E20.2.0.2"),sQuery(id+"F5.wireOp",EDGE,"E20.3.0.0"),sQuery(id+"F5.wireOp",EDGE,"E20.3.0.1"),sQuery(id+"F5.wireOp",EDGE,"E20.3.0.2"),sQuery(id+"F5.wireOp",EDGE,"E20.4.0.0"),sQuery(id+"F5.wireOp",EDGE,"E20.4.0.1"),sQuery(id+"F5.wireOp",EDGE,"E20.4.0.2"),sQuery(id+"F5.wireOp",EDGE,"E20.5.0.0"),sQuery(id+"F5.wireOp",EDGE,"E20.5.0.1"),sQuery(id+"F5.wireOp",EDGE,"E20.5.0.2"),sQuery(id+"F5.wireOp",EDGE,"E20.6.0.0"),sQuery(id+"F5.wireOp",EDGE,"E20.6.0.1"),sQuery(id+"F5.wireOp",EDGE,"E20.6.0.2"),sQuery(id+"F5.wireOp",EDGE,"E20.7.0.0"),sQuery(id+"F5.wireOp",EDGE,"E20.7.0.1"),sQuery(id+"F5.wireOp",EDGE,"E20.7.0.2"),sQuery(id+"F5.wireOp",EDGE,"E20.8.0.0"),sQuery(id+"F5.wireOp",EDGE,"E20.8.0.1"),sQuery(id+"F5.wireOp",EDGE,"E20.8.0.2"),sQuery(id+"F5.wireOp",EDGE,"E20.9.0.0"),sQuery(id+"F5.wireOp",EDGE,"E20.9.0.1"),sQuery(id+"F5.wireOp",EDGE,"E20.9.0.2"),sQuery(id+"F5.wireOp",EDGE,"E20.10.0.0"),sQuery(id+"F5.wireOp",EDGE,"E20.10.0.1"),sQuery(id+"F5.wireOp",EDGE,"E20.10.0.2"),sQuery(id+"F5.wireOp",EDGE,"E20.11.0.0"),sQuery(id+"F5.wireOp",EDGE,"E20.11.0.1"),sQuery(id+"F5.wireOp",EDGE,"E20.11.0.2"),sQuery(id+"F5.wireOp",EDGE,"E20.12.0.0"),sQuery(id+"F5.wireOp",EDGE,"E20.12.0.1"),sQuery(id+"F5.wireOp",EDGE,"E20.12.0.2"),sQuery(id+"F5.wireOp",EDGE,"E20.13.0.0"),sQuery(id+"F5.wireOp",EDGE,"E20.13.0.1"),sQuery(id+"F5.wireOp",EDGE,"E20.13.0.2"),sQuery(id+"F5.wireOp",EDGE,"E20.14.0.0"),sQuery(id+"F5.wireOp",EDGE,"E20.14.0.1"),sQuery(id+"F5.wireOp",EDGE,"E20.14.0.2"),sQuery(id+"F5.wireOp",EDGE,"E20.15.0.0"),sQuery(id+"F5.wireOp",EDGE,"E20.15.0.1"),sQuery(id+"F5.wireOp",EDGE,"E20.15.0.2"),sQuery(id+"F5.wireOp",EDGE,"E20.16.0.0"),sQuery(id+"F5.wireOp",EDGE,"E20.16.0.1"),sQuery(id+"F5.wireOp",EDGE,"E20.16.0.2"),sQuery(id+"F5.wireOp",EDGE,"E20.17.0.0"),sQuery(id+"F5.wireOp",EDGE,"E20.17.0.1"),sQuery(id+"F5.wireOp",EDGE,"E20.17.0.2"),sQuery(id+"F5.wireOp",EDGE,"E21.bottom"),sQuery(id+"F5.wireOp",EDGE,"E21.top"),sQuery(id+"F5.wireOp",EDGE,"E21.left"),sQuery(id+"F5.wireOp",EDGE,"E21.right"),sQuery(id+"F5.wireOp",EDGE,"E22.0.1.0"),sQuery(id+"F5.wireOp",EDGE,"E22.0.1.1"),sQuery(id+"F5.wireOp",EDGE,"E22.0.1.2"),sQuery(id+"F5.wireOp",EDGE,"E22.0.2.0"),sQuery(id+"F5.wireOp",EDGE,"E22.0.2.1"),sQuery(id+"F5.wireOp",EDGE,"E22.0.2.2"),sQuery(id+"F5.wireOp",EDGE,"E22.0.3.0"),sQuery(id+"F5.wireOp",EDGE,"E22.0.3.1"),sQuery(id+"F5.wireOp",EDGE,"E22.0.3.2"),sQuery(id+"F5.wireOp",EDGE,"E22.0.4.0"),sQuery(id+"F5.wireOp",EDGE,"E22.0.4.1"),sQuery(id+"F5.wireOp",EDGE,"E22.0.4.2"),sQuery(id+"F5.wireOp",EDGE,"E22.0.5.0"),sQuery(id+"F5.wireOp",EDGE,"E22.0.5.1"),sQuery(id+"F5.wireOp",EDGE,"E22.0.5.2"),sQuery(id+"F5.wireOp",EDGE,"E22.0.6.0"),sQuery(id+"F5.wireOp",EDGE,"E22.0.6.1"),sQuery(id+"F5.wireOp",EDGE,"E22.0.6.2"),sQuery(id+"F5.wireOp",EDGE,"E22.0.7.0"),sQuery(id+"F5.wireOp",EDGE,"E22.0.7.1"),sQuery(id+"F5.wireOp",EDGE,"E22.0.7.2"),sQuery(id+"F5.wireOp",EDGE,"E22.0.8.0"),sQuery(id+"F5.wireOp",EDGE,"E22.0.8.1"),sQuery(id+"F5.wireOp",EDGE,"E22.0.8.2"),sQuery(id+"F5.wireOp",EDGE,"E22.0.9.0"),sQuery(id+"F5.wireOp",EDGE,"E22.0.9.1"),sQuery(id+"F5.wireOp",EDGE,"E22.0.9.2"),sQuery(id+"F5.wireOp",EDGE,"E22.0.10.0"),sQuery(id+"F5.wireOp",EDGE,"E22.0.10.1"),sQuery(id+"F5.wireOp",EDGE,"E22.0.10.2"),sQuery(id+"F5.wireOp",EDGE,"E22.0.11.0"),sQuery(id+"F5.wireOp",EDGE,"E22.0.11.1"),sQuery(id+"F5.wireOp",EDGE,"E22.0.11.2"),sQuery(id+"F5.wireOp",EDGE,"E23.bottom"),sQuery(id+"F5.wireOp",EDGE,"E23.top"),sQuery(id+"F5.wireOp",EDGE,"E23.left"),sQuery(id+"F5.wireOp",EDGE,"E23.right"),sQuery(id+"F5.wireOp",EDGE,"E24.1.0.0"),sQuery(id+"F5.wireOp",EDGE,"E24.1.0.1"),sQuery(id+"F5.wireOp",EDGE,"E24.1.0.3"),sQuery(id+"F5.wireOp",EDGE,"E24.2.0.0"),sQuery(id+"F5.wireOp",EDGE,"E24.2.0.1"),sQuery(id+"F5.wireOp",EDGE,"E24.2.0.3"),sQuery(id+"F5.wireOp",EDGE,"E24.3.0.0"),sQuery(id+"F5.wireOp",EDGE,"E24.3.0.1"),sQuery(id+"F5.wireOp",EDGE,"E24.3.0.3"),sQuery(id+"F5.wireOp",EDGE,"E24.4.0.0"),sQuery(id+"F5.wireOp",EDGE,"E24.4.0.1"),sQuery(id+"F5.wireOp",EDGE,"E24.4.0.3"),sQuery(id+"F5.wireOp",EDGE,"E24.5.0.0"),sQuery(id+"F5.wireOp",EDGE,"E24.5.0.1"),sQuery(id+"F5.wireOp",EDGE,"E24.5.0.3"),sQuery(id+"F5.wireOp",EDGE,"E24.6.0.0"),sQuery(id+"F5.wireOp",EDGE,"E24.6.0.1"),sQuery(id+"F5.wireOp",EDGE,"E24.6.0.3"),sQuery(id+"F5.wireOp",EDGE,"E24.7.0.0"),sQuery(id+"F5.wireOp",EDGE,"E24.7.0.1"),sQuery(id+"F5.wireOp",EDGE,"E24.7.0.3"),sQuery(id+"F5.wireOp",EDGE,"E24.8.0.0"),sQuery(id+"F5.wireOp",EDGE,"E24.8.0.1"),sQuery(id+"F5.wireOp",EDGE,"E24.8.0.3"),sQuery(id+"F5.wireOp",EDGE,"E24.9.0.0"),sQuery(id+"F5.wireOp",EDGE,"E24.9.0.1"),sQuery(id+"F5.wireOp",EDGE,"E24.9.0.3"),sQuery(id+"F5.wireOp",EDGE,"E24.10.0.0"),sQuery(id+"F5.wireOp",EDGE,"E24.10.0.1"),sQuery(id+"F5.wireOp",EDGE,"E24.10.0.3"),sQuery(id+"F5.wireOp",EDGE,"E24.11.0.0"),sQuery(id+"F5.wireOp",EDGE,"E24.11.0.1"),sQuery(id+"F5.wireOp",EDGE,"E24.11.0.3"),sQuery(id+"F5.wireOp",EDGE,"E24.12.0.0"),sQuery(id+"F5.wireOp",EDGE,"E24.12.0.1"),sQuery(id+"F5.wireOp",EDGE,"E24.12.0.3"),sQuery(id+"F5.wireOp",EDGE,"E24.13.0.0"),sQuery(id+"F5.wireOp",EDGE,"E24.13.0.1"),sQuery(id+"F5.wireOp",EDGE,"E24.13.0.3"),sQuery(id+"F5.wireOp",EDGE,"E24.14.0.0"),sQuery(id+"F5.wireOp",EDGE,"E24.14.0.1"),sQuery(id+"F5.wireOp",EDGE,"E24.14.0.3"),sQuery(id+"F5.wireOp",EDGE,"E24.15.0.0"),sQuery(id+"F5.wireOp",EDGE,"E24.15.0.1"),sQuery(id+"F5.wireOp",EDGE,"E24.15.0.3"),sQuery(id+"F5.wireOp",EDGE,"E24.16.0.0"),sQuery(id+"F5.wireOp",EDGE,"E24.16.0.1"),sQuery(id+"F5.wireOp",EDGE,"E24.16.0.3"),sQuery(id+"F5.wireOp",EDGE,"E24.17.0.0"),sQuery(id+"F5.wireOp",EDGE,"E24.17.0.1"),sQuery(id+"F5.wireOp",EDGE,"E24.17.0.3"),sQuery(id+"F5.wireOp",EDGE,"E25.bottom"),sQuery(id+"F5.wireOp",EDGE,"E25.top"),sQuery(id+"F5.wireOp",EDGE,"E25.left"),sQuery(id+"F5.wireOp",EDGE,"E25.right"),sQuery(id+"F5.wireOp",EDGE,"E26.0.1.1"),sQuery(id+"F5.wireOp",EDGE,"E26.0.1.2"),sQuery(id+"F5.wireOp",EDGE,"E26.0.1.3"),sQuery(id+"F5.wireOp",EDGE,"E26.0.2.1"),sQuery(id+"F5.wireOp",EDGE,"E26.0.2.2"),sQuery(id+"F5.wireOp",EDGE,"E26.0.2.3"),sQuery(id+"F5.wireOp",EDGE,"E26.0.3.1"),sQuery(id+"F5.wireOp",EDGE,"E26.0.3.2"),sQuery(id+"F5.wireOp",EDGE,"E26.0.3.3"),sQuery(id+"F5.wireOp",EDGE,"E26.0.4.1"),sQuery(id+"F5.wireOp",EDGE,"E26.0.4.2"),sQuery(id+"F5.wireOp",EDGE,"E26.0.4.3"),sQuery(id+"F5.wireOp",EDGE,"E26.0.5.1"),sQuery(id+"F5.wireOp",EDGE,"E26.0.5.2"),sQuery(id+"F5.wireOp",EDGE,"E26.0.5.3"),sQuery(id+"F5.wireOp",EDGE,"E26.0.6.1"),sQuery(id+"F5.wireOp",EDGE,"E26.0.6.2"),sQuery(id+"F5.wireOp",EDGE,"E26.0.6.3"),sQuery(id+"F5.wireOp",EDGE,"E26.0.7.1"),sQuery(id+"F5.wireOp",EDGE,"E26.0.7.2"),sQuery(id+"F5.wireOp",EDGE,"E26.0.7.3"),sQuery(id+"F5.wireOp",EDGE,"E26.0.8.1"),sQuery(id+"F5.wireOp",EDGE,"E26.0.8.2"),sQuery(id+"F5.wireOp",EDGE,"E26.0.8.3"),sQuery(id+"F5.wireOp",EDGE,"E26.0.9.1"),sQuery(id+"F5.wireOp",EDGE,"E26.0.9.2"),sQuery(id+"F5.wireOp",EDGE,"E26.0.9.3"),sQuery(id+"F5.wireOp",EDGE,"E26.0.10.1"),sQuery(id+"F5.wireOp",EDGE,"E26.0.10.2"),sQuery(id+"F5.wireOp",EDGE,"E26.0.10.3"),sQuery(id+"F5.wireOp",EDGE,"E26.0.11.1"),sQuery(id+"F5.wireOp",EDGE,"E26.0.11.2"),sQuery(id+"F5.wireOp",EDGE,"E26.0.11.3")])]});
            var Q2;
            Q2=makeQuery(id+"F10.opExtrude","SWEPT_BODY",BODY,{"disambiguationData":[OSD([sQuery(id+"F4.wireOp",EDGE,"E15.bottom"),sQuery(id+"F4.wireOp",EDGE,"E15.top"),sQuery(id+"F4.wireOp",EDGE,"E15.left"),sQuery(id+"F4.wireOp",EDGE,"E15.right")])]});
            var Q3;
            Q3=makeQuery(id+"F10.opExtrude","SWEPT_BODY",BODY,{"disambiguationData":[OSD([sQuery(id+"F4.wireOp",EDGE,"E13.bottom"),sQuery(id+"F4.wireOp",EDGE,"E13.top"),sQuery(id+"F4.wireOp",EDGE,"E13.left"),sQuery(id+"F4.wireOp",EDGE,"E13.right")])]});
            var Q4;
            Q4=makeQuery(id+"F10.opExtrude","SWEPT_BODY",BODY,{"disambiguationData":[OSD([sQuery(id+"F4.wireOp",EDGE,"E14.bottom"),sQuery(id+"F4.wireOp",EDGE,"E14.top"),sQuery(id+"F4.wireOp",EDGE,"E14.left"),sQuery(id+"F4.wireOp",EDGE,"E14.right")])]});
            var Q5;
            Q5=makeQuery(id+"F12.opExtrude","SWEPT_BODY",BODY,{"disambiguationData":[OSD([sQuery(id+"F3.wireOp",EDGE,"E8.bottom"),sQuery(id+"F3.wireOp",EDGE,"E8.top"),sQuery(id+"F3.wireOp",EDGE,"E8.left"),sQuery(id+"F3.wireOp",EDGE,"E8.right")])]});
            var Q6;
            Q6=makeQuery(id+"F10.opExtrude","SWEPT_BODY",BODY,{"disambiguationData":[OSD([sQuery(id+"F4.wireOp",EDGE,"E16.bottom"),sQuery(id+"F4.wireOp",EDGE,"E16.top"),sQuery(id+"F4.wireOp",EDGE,"E16.left"),sQuery(id+"F4.wireOp",EDGE,"E16.right")])]});
            var Q7;
            Q7=makeQuery(id+"F10.opExtrude","SWEPT_BODY",BODY,{"disambiguationData":[OSD([sQuery(id+"F4.wireOp",EDGE,"E17.bottom"),sQuery(id+"F4.wireOp",EDGE,"E17.top"),sQuery(id+"F4.wireOp",EDGE,"E17.left"),sQuery(id+"F4.wireOp",EDGE,"E17.right")])]});
            var Q8;
            Q8=makeQuery(id+"F12.opExtrude","SWEPT_BODY",BODY,{"disambiguationData":[OSD([sQuery(id+"F3.wireOp",EDGE,"E9.bottom"),sQuery(id+"F3.wireOp",EDGE,"E9.top"),sQuery(id+"F3.wireOp",EDGE,"E9.left"),sQuery(id+"F3.wireOp",EDGE,"E9.right")])]});
            var Q9;
            Q9=makeQuery(id+"F12.opExtrude","SWEPT_BODY",BODY,{"disambiguationData":[OSD([sQuery(id+"F3.wireOp",EDGE,"E10.bottom"),sQuery(id+"F3.wireOp",EDGE,"E10.top"),sQuery(id+"F3.wireOp",EDGE,"E10.left"),sQuery(id+"F3.wireOp",EDGE,"E10.right")])]});
            var Q10;
            Q10=makeQuery(id+"F12.opExtrude","SWEPT_BODY",BODY,{"disambiguationData":[OSD([sQuery(id+"F3.wireOp",EDGE,"E11.bottom"),sQuery(id+"F3.wireOp",EDGE,"E11.top"),sQuery(id+"F3.wireOp",EDGE,"E11.left"),sQuery(id+"F3.wireOp",EDGE,"E11.right")])]});
            var Q11;
            Q11=makeQuery(id+"F12.opExtrude","SWEPT_BODY",BODY,{"disambiguationData":[OSD([sQuery(id+"F3.wireOp",EDGE,"E12.bottom"),sQuery(id+"F3.wireOp",EDGE,"E12.top"),sQuery(id+"F3.wireOp",EDGE,"E12.left"),sQuery(id+"F3.wireOp",EDGE,"E12.right")])]});
            booleanBodies(context, id + "F14", {"operationType" : BooleanOperationType.SUBTRACTION, "tools" : qUnion([Q0, Q1]), "targets" : qUnion([Q2, Q3, Q4, Q5, Q6, Q7, Q8, Q9, Q10, Q11]), "keepTools" : true});
        }
    });
